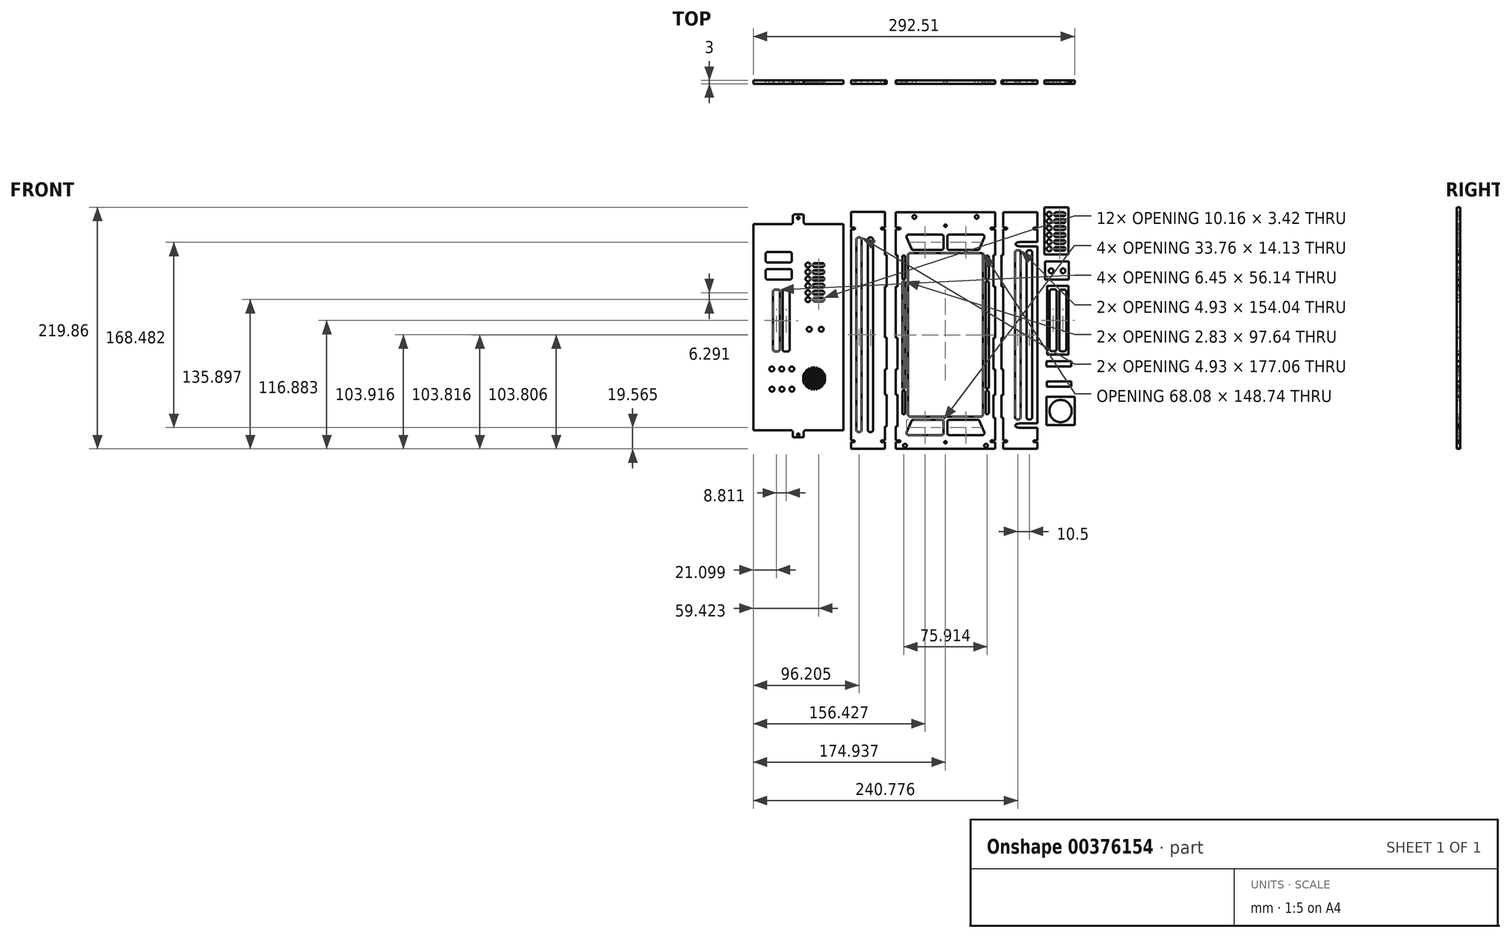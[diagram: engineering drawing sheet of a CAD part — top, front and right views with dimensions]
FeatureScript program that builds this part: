
annotation { "Feature Type Name" : "Feature", "Feature Type Description" : "" }
export const myFeature = defineFeature(function(context is Context, id is Id, definition is map)
    precondition{}
    {
        {
            var Q0;
            Q0=qCreatedBy(makeId("Front.planeOp"),FACE);
            var sketch = newSketch(context, id + "F0", { "sketchPlane" : qUnion([Q0])});
            skCircle(sketch, "E0", {"center": v(131.55, 198.45) * mm, "radius": 2.2 * mm});
            skCircle(sketch, "E1", {"center": v(131.55, 204.74) * mm, "radius": 2.2 * mm});
            skCircle(sketch, "E2", {"center": v(131.55, 211.03) * mm, "radius": 2.2 * mm});
            skCircle(sketch, "E3", {"center": v(131.55, 217.32) * mm, "radius": 2.2 * mm});
            skCircle(sketch, "E4", {"center": v(131.55, 223.61) * mm, "radius": 2.2 * mm});
            skCircle(sketch, "E5", {"center": v(131.55, 229.9) * mm, "radius": 2.2 * mm});
            skCircle(sketch, "E6", {"center": v(133.32, 178.42) * mm, "radius": 2.2 * mm});
            skCircle(sketch, "E7", {"center": v(144.17, 178.42) * mm, "radius": 2.2 * mm});
            skCircle(sketch, "E8", {"center": v(141.9, 50.82) * mm, "radius": 10.16 * mm});
            skCircle(sketch, "E9", {"center": v(37.16, 219.53) * mm, "radius": 1.07 * mm});
            skCircle(sketch, "E10", {"center": v(37.13, 22.37) * mm, "radius": 1.07 * mm});
            skCircle(sketch, "E11", {"center": v(-86.74, 125.22) * mm, "radius": 2.2 * mm});
            skCircle(sketch, "E12", {"center": v(-75.89, 125.22) * mm, "radius": 2.2 * mm});
            skCircle(sketch, "E13", {"center": v(-87.97, 152.24) * mm, "radius": 2.2 * mm});
            skCircle(sketch, "E14", {"center": v(-87.97, 158.53) * mm, "radius": 2.2 * mm});
            skCircle(sketch, "E15", {"center": v(-87.97, 164.82) * mm, "radius": 2.2 * mm});
            skCircle(sketch, "E16", {"center": v(-87.97, 171.1) * mm, "radius": 2.2 * mm});
            skCircle(sketch, "E17", {"center": v(-87.97, 177.4) * mm, "radius": 2.2 * mm});
            skCircle(sketch, "E18", {"center": v(-87.97, 183.7) * mm, "radius": 2.2 * mm});
            skCircle(sketch, "E19", {"center": v(-96.77, 226.54) * mm, "radius": 1.07 * mm});
            skCircle(sketch, "E20", {"center": v(-96.8, 29.38) * mm, "radius": 1.07 * mm});
            skCircle(sketch, "E21", {"center": v(-102.71, 89.08) * mm, "radius": 2.2 * mm});
            skCircle(sketch, "E22", {"center": v(-111.79, 89.08) * mm, "radius": 2.2 * mm});
            skCircle(sketch, "E23", {"center": v(-120.86, 89.08) * mm, "radius": 2.2 * mm});
            skCircle(sketch, "E24", {"center": v(-120.72, 70.7) * mm, "radius": 2.2 * mm});
            skCircle(sketch, "E25", {"center": v(-111.65, 70.7) * mm, "radius": 2.2 * mm});
            skCircle(sketch, "E26", {"center": v(-102.57, 70.7) * mm, "radius": 2.2 * mm});
            skLineSegment(sketch, "E27", {"start": v(73.7, 191.17) * mm, "end": v(73.7, 171.98) * mm});
            skArc(sketch, "E28", {"start": v(73.7, 171.98) * mm, "mid": v(74.01, 171.22) * mm, "end": v(74.77, 170.91) * mm});
            skLineSegment(sketch, "E29", {"start": v(74.77, 170.91) * mm, "end": v(75.46, 170.91) * mm});
            skArc(sketch, "E30", {"start": v(75.46, 170.91) * mm, "mid": v(76.21, 171.22) * mm, "end": v(76.53, 171.98) * mm});
            skLineSegment(sketch, "E31", {"start": v(76.53, 171.98) * mm, "end": v(76.53, 191.17) * mm});
            skArc(sketch, "E32", {"start": v(76.53, 191.17) * mm, "mid": v(76.21, 191.93) * mm, "end": v(75.46, 192.24) * mm});
            skLineSegment(sketch, "E33", {"start": v(75.46, 192.24) * mm, "end": v(74.77, 192.24) * mm});
            skArc(sketch, "E34", {"start": v(74.77, 192.24) * mm, "mid": v(74.01, 191.93) * mm, "end": v(73.7, 191.17) * mm});
            skLineSegment(sketch, "E35", {"start": v(73.7, 167.9) * mm, "end": v(73.7, 72.4) * mm});
            skArc(sketch, "E36", {"start": v(73.7, 72.4) * mm, "mid": v(74.01, 71.64) * mm, "end": v(74.77, 71.32) * mm});
            skLineSegment(sketch, "E37", {"start": v(74.77, 71.32) * mm, "end": v(75.46, 71.32) * mm});
            skArc(sketch, "E38", {"start": v(75.46, 71.32) * mm, "mid": v(76.21, 71.64) * mm, "end": v(76.53, 72.4) * mm});
            skLineSegment(sketch, "E39", {"start": v(76.53, 72.4) * mm, "end": v(76.53, 167.9) * mm});
            skArc(sketch, "E40", {"start": v(76.53, 167.9) * mm, "mid": v(76.21, 168.65) * mm, "end": v(75.46, 168.97) * mm});
            skLineSegment(sketch, "E41", {"start": v(75.46, 168.97) * mm, "end": v(74.77, 168.97) * mm});
            skArc(sketch, "E42", {"start": v(74.77, 168.97) * mm, "mid": v(74.01, 168.65) * mm, "end": v(73.7, 167.9) * mm});
            skLineSegment(sketch, "E43", {"start": v(73.7, 68.3) * mm, "end": v(73.7, 49.12) * mm});
            skArc(sketch, "E44", {"start": v(73.7, 49.12) * mm, "mid": v(74.01, 48.36) * mm, "end": v(74.77, 48.05) * mm});
            skLineSegment(sketch, "E45", {"start": v(74.77, 48.05) * mm, "end": v(75.46, 48.05) * mm});
            skArc(sketch, "E46", {"start": v(75.46, 48.05) * mm, "mid": v(76.21, 48.36) * mm, "end": v(76.53, 49.12) * mm});
            skLineSegment(sketch, "E47", {"start": v(76.53, 49.12) * mm, "end": v(76.53, 68.3) * mm});
            skArc(sketch, "E48", {"start": v(76.53, 68.3) * mm, "mid": v(76.21, 69.07) * mm, "end": v(75.46, 69.38) * mm});
            skLineSegment(sketch, "E49", {"start": v(75.46, 69.38) * mm, "end": v(74.77, 69.38) * mm});
            skArc(sketch, "E50", {"start": v(74.77, 69.38) * mm, "mid": v(74.01, 69.07) * mm, "end": v(73.7, 68.3) * mm});
            skArc(sketch, "E51", {"start": v(0.61, 68.3) * mm, "mid": v(0.3, 69.07) * mm, "end": v(-0.46, 69.38) * mm});
            skLineSegment(sketch, "E52", {"start": v(-0.46, 69.38) * mm, "end": v(-1.14, 69.38) * mm});
            skArc(sketch, "E53", {"start": v(-1.14, 69.38) * mm, "mid": v(-1.9, 69.07) * mm, "end": v(-2.21, 68.3) * mm});
            skLineSegment(sketch, "E54", {"start": v(-2.21, 68.3) * mm, "end": v(-2.21, 49.12) * mm});
            skArc(sketch, "E55", {"start": v(-2.21, 49.12) * mm, "mid": v(-1.9, 48.36) * mm, "end": v(-1.14, 48.05) * mm});
            skLineSegment(sketch, "E56", {"start": v(-1.14, 48.05) * mm, "end": v(-0.46, 48.05) * mm});
            skArc(sketch, "E57", {"start": v(-0.46, 48.05) * mm, "mid": v(0.3, 48.36) * mm, "end": v(0.61, 49.12) * mm});
            skLineSegment(sketch, "E58", {"start": v(0.61, 49.12) * mm, "end": v(0.61, 68.3) * mm});
            skArc(sketch, "E59", {"start": v(0.61, 167.9) * mm, "mid": v(0.3, 168.65) * mm, "end": v(-0.46, 168.97) * mm});
            skLineSegment(sketch, "E60", {"start": v(-0.46, 168.97) * mm, "end": v(-1.14, 168.97) * mm});
            skArc(sketch, "E61", {"start": v(-1.14, 168.97) * mm, "mid": v(-1.9, 168.65) * mm, "end": v(-2.21, 167.9) * mm});
            skLineSegment(sketch, "E62", {"start": v(-2.21, 167.9) * mm, "end": v(-2.21, 72.4) * mm});
            skArc(sketch, "E63", {"start": v(-2.21, 72.4) * mm, "mid": v(-1.9, 71.64) * mm, "end": v(-1.14, 71.32) * mm});
            skLineSegment(sketch, "E64", {"start": v(-1.14, 71.32) * mm, "end": v(-0.46, 71.32) * mm});
            skArc(sketch, "E65", {"start": v(-0.46, 71.32) * mm, "mid": v(0.3, 71.64) * mm, "end": v(0.61, 72.4) * mm});
            skLineSegment(sketch, "E66", {"start": v(0.61, 72.4) * mm, "end": v(0.61, 167.9) * mm});
            skArc(sketch, "E67", {"start": v(0.61, 191.17) * mm, "mid": v(0.3, 191.93) * mm, "end": v(-0.46, 192.24) * mm});
            skLineSegment(sketch, "E68", {"start": v(-0.46, 192.24) * mm, "end": v(-1.14, 192.24) * mm});
            skArc(sketch, "E69", {"start": v(-1.14, 192.24) * mm, "mid": v(-1.9, 191.93) * mm, "end": v(-2.21, 191.17) * mm});
            skLineSegment(sketch, "E70", {"start": v(-2.21, 191.17) * mm, "end": v(-2.21, 171.98) * mm});
            skArc(sketch, "E71", {"start": v(-2.21, 171.98) * mm, "mid": v(-1.9, 171.22) * mm, "end": v(-1.14, 170.91) * mm});
            skLineSegment(sketch, "E72", {"start": v(-1.14, 170.91) * mm, "end": v(-0.46, 170.91) * mm});
            skArc(sketch, "E73", {"start": v(-0.46, 170.91) * mm, "mid": v(0.3, 171.22) * mm, "end": v(0.61, 171.98) * mm});
            skLineSegment(sketch, "E74", {"start": v(0.61, 171.98) * mm, "end": v(0.61, 191.17) * mm});
            skLineSegment(sketch, "E75", {"start": v(8.26, 197.32) * mm, "end": v(33.27, 197.32) * mm});
            skArc(sketch, "E76", {"start": v(33.27, 197.32) * mm, "mid": v(33.63, 197.35) * mm, "end": v(33.98, 197.42) * mm});
            skArc(sketch, "E77", {"start": v(33.98, 197.42) * mm, "mid": v(34.3, 197.53) * mm, "end": v(34.6, 197.69) * mm});
            skArc(sketch, "E78", {"start": v(34.6, 197.69) * mm, "mid": v(34.85, 197.86) * mm, "end": v(35.06, 198.06) * mm});
            skArc(sketch, "E79", {"start": v(35.06, 198.06) * mm, "mid": v(35.22, 198.26) * mm, "end": v(35.35, 198.48) * mm});
            skArc(sketch, "E80", {"start": v(35.35, 198.48) * mm, "mid": v(35.44, 198.7) * mm, "end": v(35.5, 198.92) * mm});
            skArc(sketch, "E81", {"start": v(35.5, 198.92) * mm, "mid": v(35.52, 199.07) * mm, "end": v(35.53, 199.21) * mm});
            skLineSegment(sketch, "E82", {"start": v(35.53, 199.21) * mm, "end": v(35.53, 209.56) * mm});
            skArc(sketch, "E83", {"start": v(35.53, 209.56) * mm, "mid": v(35.51, 209.79) * mm, "end": v(35.46, 210) * mm});
            skArc(sketch, "E84", {"start": v(35.46, 210) * mm, "mid": v(35.38, 210.22) * mm, "end": v(35.28, 210.43) * mm});
            skArc(sketch, "E85", {"start": v(35.28, 210.43) * mm, "mid": v(35.12, 210.65) * mm, "end": v(34.93, 210.84) * mm});
            skArc(sketch, "E86", {"start": v(34.93, 210.84) * mm, "mid": v(34.7, 211.03) * mm, "end": v(34.43, 211.18) * mm});
            skArc(sketch, "E87", {"start": v(34.43, 211.18) * mm, "mid": v(34.11, 211.32) * mm, "end": v(33.78, 211.4) * mm});
            skArc(sketch, "E88", {"start": v(33.78, 211.4) * mm, "mid": v(33.52, 211.44) * mm, "end": v(33.27, 211.45) * mm});
            skLineSegment(sketch, "E89", {"start": v(33.27, 211.45) * mm, "end": v(4.02, 211.45) * mm});
            skArc(sketch, "E90", {"start": v(4.02, 211.45) * mm, "mid": v(3.66, 211.43) * mm, "end": v(3.31, 211.35) * mm});
            skArc(sketch, "E91", {"start": v(3.31, 211.35) * mm, "mid": v(3, 211.24) * mm, "end": v(2.7, 211.09) * mm});
            skArc(sketch, "E92", {"start": v(2.7, 211.09) * mm, "mid": v(2.45, 210.91) * mm, "end": v(2.23, 210.7) * mm});
            skArc(sketch, "E93", {"start": v(2.23, 210.7) * mm, "mid": v(2.07, 210.5) * mm, "end": v(1.94, 210.29) * mm});
            skArc(sketch, "E94", {"start": v(1.94, 210.29) * mm, "mid": v(1.85, 210.07) * mm, "end": v(1.8, 209.85) * mm});
            skArc(sketch, "E95", {"start": v(1.8, 209.85) * mm, "mid": v(1.77, 209.7) * mm, "end": v(1.77, 209.56) * mm});
            skLineSegment(sketch, "E96", {"start": v(1.77, 209.56) * mm, "end": v(1.77, 209.55) * mm});
            skArc(sketch, "E97", {"start": v(1.77, 209.55) * mm, "mid": v(1.78, 209.34) * mm, "end": v(1.82, 209.14) * mm});
            skArc(sketch, "E98", {"start": v(1.82, 209.14) * mm, "mid": v(1.85, 209.04) * mm, "end": v(1.89, 208.95) * mm});
            skLineSegment(sketch, "E99", {"start": v(1.89, 208.95) * mm, "end": v(6.13, 198.6) * mm});
            skArc(sketch, "E100", {"start": v(6.13, 198.6) * mm, "mid": v(6.23, 198.38) * mm, "end": v(6.37, 198.18) * mm});
            skArc(sketch, "E101", {"start": v(6.37, 198.18) * mm, "mid": v(6.56, 197.97) * mm, "end": v(6.77, 197.8) * mm});
            skArc(sketch, "E102", {"start": v(6.77, 197.8) * mm, "mid": v(7.05, 197.62) * mm, "end": v(7.34, 197.49) * mm});
            skArc(sketch, "E103", {"start": v(7.34, 197.49) * mm, "mid": v(7.68, 197.39) * mm, "end": v(8.04, 197.33) * mm});
            skArc(sketch, "E104", {"start": v(8.04, 197.33) * mm, "mid": v(8.15, 197.33) * mm, "end": v(8.26, 197.32) * mm});
            skLineSegment(sketch, "E105", {"start": v(70.3, 211.45) * mm, "end": v(41.04, 211.45) * mm});
            skArc(sketch, "E106", {"start": v(41.04, 211.45) * mm, "mid": v(40.68, 211.43) * mm, "end": v(40.33, 211.35) * mm});
            skArc(sketch, "E107", {"start": v(40.33, 211.35) * mm, "mid": v(40.01, 211.24) * mm, "end": v(39.71, 211.09) * mm});
            skArc(sketch, "E108", {"start": v(39.71, 211.09) * mm, "mid": v(39.47, 210.91) * mm, "end": v(39.25, 210.7) * mm});
            skArc(sketch, "E109", {"start": v(39.25, 210.7) * mm, "mid": v(39.1, 210.5) * mm, "end": v(38.96, 210.29) * mm});
            skArc(sketch, "E110", {"start": v(38.96, 210.29) * mm, "mid": v(38.87, 210.07) * mm, "end": v(38.81, 209.85) * mm});
            skArc(sketch, "E111", {"start": v(38.81, 209.85) * mm, "mid": v(38.8, 209.7) * mm, "end": v(38.79, 209.56) * mm});
            skLineSegment(sketch, "E112", {"start": v(38.79, 209.56) * mm, "end": v(38.79, 199.21) * mm});
            skArc(sketch, "E113", {"start": v(38.79, 199.21) * mm, "mid": v(38.8, 198.99) * mm, "end": v(38.85, 198.77) * mm});
            skArc(sketch, "E114", {"start": v(38.85, 198.77) * mm, "mid": v(38.93, 198.55) * mm, "end": v(39.04, 198.34) * mm});
            skArc(sketch, "E115", {"start": v(39.04, 198.34) * mm, "mid": v(39.2, 198.13) * mm, "end": v(39.38, 197.93) * mm});
            skArc(sketch, "E116", {"start": v(39.38, 197.93) * mm, "mid": v(39.62, 197.74) * mm, "end": v(39.89, 197.59) * mm});
            skArc(sketch, "E117", {"start": v(39.89, 197.59) * mm, "mid": v(40.2, 197.46) * mm, "end": v(40.54, 197.37) * mm});
            skArc(sketch, "E118", {"start": v(40.54, 197.37) * mm, "mid": v(40.79, 197.33) * mm, "end": v(41.04, 197.32) * mm});
            skLineSegment(sketch, "E119", {"start": v(41.04, 197.32) * mm, "end": v(66.05, 197.32) * mm});
            skArc(sketch, "E120", {"start": v(66.05, 197.32) * mm, "mid": v(66.41, 197.35) * mm, "end": v(66.76, 197.42) * mm});
            skArc(sketch, "E121", {"start": v(66.76, 197.42) * mm, "mid": v(67.08, 197.53) * mm, "end": v(67.37, 197.68) * mm});
            skArc(sketch, "E122", {"start": v(67.37, 197.68) * mm, "mid": v(67.61, 197.85) * mm, "end": v(67.83, 198.05) * mm});
            skArc(sketch, "E123", {"start": v(67.83, 198.05) * mm, "mid": v(68, 198.26) * mm, "end": v(68.13, 198.48) * mm});
            skArc(sketch, "E124", {"start": v(68.13, 198.48) * mm, "mid": v(68.16, 198.54) * mm, "end": v(68.19, 198.6) * mm});
            skLineSegment(sketch, "E125", {"start": v(68.19, 198.6) * mm, "end": v(72.43, 208.95) * mm});
            skArc(sketch, "E126", {"start": v(72.43, 208.95) * mm, "mid": v(72.5, 209.16) * mm, "end": v(72.54, 209.39) * mm});
            skArc(sketch, "E127", {"start": v(72.54, 209.39) * mm, "mid": v(72.55, 209.6) * mm, "end": v(72.53, 209.82) * mm});
            skArc(sketch, "E128", {"start": v(72.53, 209.82) * mm, "mid": v(72.47, 210.04) * mm, "end": v(72.4, 210.25) * mm});
            skArc(sketch, "E129", {"start": v(72.4, 210.25) * mm, "mid": v(72.27, 210.47) * mm, "end": v(72.11, 210.67) * mm});
            skArc(sketch, "E130", {"start": v(72.11, 210.67) * mm, "mid": v(71.9, 210.88) * mm, "end": v(71.68, 211.05) * mm});
            skArc(sketch, "E131", {"start": v(71.68, 211.05) * mm, "mid": v(71.38, 211.22) * mm, "end": v(71.07, 211.33) * mm});
            skLineSegment(sketch, "E132", {"start": v(71.07, 211.33) * mm, "end": v(71.02, 211.35) * mm});
            skArc(sketch, "E133", {"start": v(71.02, 211.35) * mm, "mid": v(70.69, 211.42) * mm, "end": v(70.35, 211.45) * mm});
            skLineSegment(sketch, "E134", {"start": v(70.35, 211.45) * mm, "end": v(70.3, 211.45) * mm});
            skArc(sketch, "E135", {"start": v(70.3, 28.84) * mm, "mid": v(70.65, 28.86) * mm, "end": v(71, 28.94) * mm});
            skArc(sketch, "E136", {"start": v(71, 28.94) * mm, "mid": v(71.32, 29.05) * mm, "end": v(71.62, 29.2) * mm});
            skArc(sketch, "E137", {"start": v(71.62, 29.2) * mm, "mid": v(71.87, 29.38) * mm, "end": v(72.08, 29.58) * mm});
            skArc(sketch, "E138", {"start": v(72.08, 29.58) * mm, "mid": v(72.24, 29.78) * mm, "end": v(72.37, 30) * mm});
            skArc(sketch, "E139", {"start": v(72.37, 30) * mm, "mid": v(72.46, 30.22) * mm, "end": v(72.52, 30.44) * mm});
            skArc(sketch, "E140", {"start": v(72.52, 30.44) * mm, "mid": v(72.54, 30.59) * mm, "end": v(72.55, 30.73) * mm});
            skArc(sketch, "E141", {"start": v(72.55, 30.73) * mm, "mid": v(72.53, 30.94) * mm, "end": v(72.5, 31.15) * mm});
            skArc(sketch, "E142", {"start": v(72.5, 31.15) * mm, "mid": v(72.46, 31.24) * mm, "end": v(72.43, 31.34) * mm});
            skLineSegment(sketch, "E143", {"start": v(72.43, 31.34) * mm, "end": v(68.19, 41.7) * mm});
            skArc(sketch, "E144", {"start": v(68.19, 41.7) * mm, "mid": v(68.08, 41.9) * mm, "end": v(67.94, 42.11) * mm});
            skArc(sketch, "E145", {"start": v(67.94, 42.11) * mm, "mid": v(67.76, 42.32) * mm, "end": v(67.54, 42.5) * mm});
            skArc(sketch, "E146", {"start": v(67.54, 42.5) * mm, "mid": v(67.27, 42.67) * mm, "end": v(66.97, 42.8) * mm});
            skArc(sketch, "E147", {"start": v(66.97, 42.8) * mm, "mid": v(66.63, 42.9) * mm, "end": v(66.28, 42.96) * mm});
            skArc(sketch, "E148", {"start": v(66.28, 42.96) * mm, "mid": v(66.16, 42.97) * mm, "end": v(66.05, 42.97) * mm});
            skLineSegment(sketch, "E149", {"start": v(66.05, 42.97) * mm, "end": v(41.04, 42.97) * mm});
            skArc(sketch, "E150", {"start": v(41.04, 42.97) * mm, "mid": v(40.68, 42.95) * mm, "end": v(40.33, 42.87) * mm});
            skArc(sketch, "E151", {"start": v(40.33, 42.87) * mm, "mid": v(40.01, 42.76) * mm, "end": v(39.71, 42.6) * mm});
            skArc(sketch, "E152", {"start": v(39.71, 42.6) * mm, "mid": v(39.47, 42.43) * mm, "end": v(39.25, 42.23) * mm});
            skArc(sketch, "E153", {"start": v(39.25, 42.23) * mm, "mid": v(39.1, 42.03) * mm, "end": v(38.96, 41.8) * mm});
            skArc(sketch, "E154", {"start": v(38.96, 41.8) * mm, "mid": v(38.87, 41.6) * mm, "end": v(38.81, 41.37) * mm});
            skArc(sketch, "E155", {"start": v(38.81, 41.37) * mm, "mid": v(38.8, 41.22) * mm, "end": v(38.79, 41.08) * mm});
            skLineSegment(sketch, "E156", {"start": v(38.79, 41.08) * mm, "end": v(38.79, 30.73) * mm});
            skArc(sketch, "E157", {"start": v(38.79, 30.73) * mm, "mid": v(38.8, 30.5) * mm, "end": v(38.85, 30.29) * mm});
            skArc(sketch, "E158", {"start": v(38.85, 30.29) * mm, "mid": v(38.93, 30.07) * mm, "end": v(39.04, 29.86) * mm});
            skArc(sketch, "E159", {"start": v(39.04, 29.86) * mm, "mid": v(39.2, 29.64) * mm, "end": v(39.38, 29.45) * mm});
            skArc(sketch, "E160", {"start": v(39.38, 29.45) * mm, "mid": v(39.62, 29.26) * mm, "end": v(39.89, 29.1) * mm});
            skArc(sketch, "E161", {"start": v(39.89, 29.1) * mm, "mid": v(40.2, 28.98) * mm, "end": v(40.54, 28.89) * mm});
            skArc(sketch, "E162", {"start": v(40.54, 28.89) * mm, "mid": v(40.79, 28.85) * mm, "end": v(41.04, 28.84) * mm});
            skLineSegment(sketch, "E163", {"start": v(41.04, 28.84) * mm, "end": v(70.3, 28.84) * mm});
            skLineSegment(sketch, "E164", {"start": v(4.02, 28.84) * mm, "end": v(33.27, 28.84) * mm});
            skArc(sketch, "E165", {"start": v(33.27, 28.84) * mm, "mid": v(33.63, 28.86) * mm, "end": v(33.98, 28.94) * mm});
            skArc(sketch, "E166", {"start": v(33.98, 28.94) * mm, "mid": v(34.3, 29.05) * mm, "end": v(34.6, 29.2) * mm});
            skArc(sketch, "E167", {"start": v(34.6, 29.2) * mm, "mid": v(34.85, 29.38) * mm, "end": v(35.06, 29.58) * mm});
            skArc(sketch, "E168", {"start": v(35.06, 29.58) * mm, "mid": v(35.22, 29.78) * mm, "end": v(35.35, 30) * mm});
            skArc(sketch, "E169", {"start": v(35.35, 30) * mm, "mid": v(35.44, 30.22) * mm, "end": v(35.5, 30.44) * mm});
            skArc(sketch, "E170", {"start": v(35.5, 30.44) * mm, "mid": v(35.52, 30.59) * mm, "end": v(35.53, 30.73) * mm});
            skLineSegment(sketch, "E171", {"start": v(35.53, 30.73) * mm, "end": v(35.53, 41.08) * mm});
            skArc(sketch, "E172", {"start": v(35.53, 41.08) * mm, "mid": v(35.51, 41.3) * mm, "end": v(35.46, 41.52) * mm});
            skArc(sketch, "E173", {"start": v(35.46, 41.52) * mm, "mid": v(35.38, 41.74) * mm, "end": v(35.28, 41.95) * mm});
            skArc(sketch, "E174", {"start": v(35.28, 41.95) * mm, "mid": v(35.12, 42.17) * mm, "end": v(34.93, 42.36) * mm});
            skArc(sketch, "E175", {"start": v(34.93, 42.36) * mm, "mid": v(34.7, 42.55) * mm, "end": v(34.43, 42.7) * mm});
            skArc(sketch, "E176", {"start": v(34.43, 42.7) * mm, "mid": v(34.11, 42.83) * mm, "end": v(33.78, 42.92) * mm});
            skArc(sketch, "E177", {"start": v(33.78, 42.92) * mm, "mid": v(33.52, 42.96) * mm, "end": v(33.27, 42.97) * mm});
            skLineSegment(sketch, "E178", {"start": v(33.27, 42.97) * mm, "end": v(8.26, 42.97) * mm});
            skArc(sketch, "E179", {"start": v(8.26, 42.97) * mm, "mid": v(7.9, 42.94) * mm, "end": v(7.53, 42.86) * mm});
            skArc(sketch, "E180", {"start": v(7.53, 42.86) * mm, "mid": v(7.21, 42.75) * mm, "end": v(6.91, 42.6) * mm});
            skArc(sketch, "E181", {"start": v(6.91, 42.6) * mm, "mid": v(6.68, 42.43) * mm, "end": v(6.47, 42.23) * mm});
            skArc(sketch, "E182", {"start": v(6.47, 42.23) * mm, "mid": v(6.31, 42.03) * mm, "end": v(6.18, 41.81) * mm});
            skArc(sketch, "E183", {"start": v(6.18, 41.81) * mm, "mid": v(6.15, 41.75) * mm, "end": v(6.13, 41.7) * mm});
            skLineSegment(sketch, "E184", {"start": v(6.13, 41.7) * mm, "end": v(1.89, 31.34) * mm});
            skArc(sketch, "E185", {"start": v(1.89, 31.34) * mm, "mid": v(1.82, 31.15) * mm, "end": v(1.78, 30.95) * mm});
            skArc(sketch, "E186", {"start": v(1.78, 30.95) * mm, "mid": v(1.77, 30.84) * mm, "end": v(1.77, 30.73) * mm});
            skArc(sketch, "E187", {"start": v(1.77, 30.73) * mm, "mid": v(1.78, 30.5) * mm, "end": v(1.83, 30.29) * mm});
            skArc(sketch, "E188", {"start": v(1.83, 30.29) * mm, "mid": v(1.9, 30.07) * mm, "end": v(2.02, 29.86) * mm});
            skArc(sketch, "E189", {"start": v(2.02, 29.86) * mm, "mid": v(2.18, 29.64) * mm, "end": v(2.36, 29.45) * mm});
            skArc(sketch, "E190", {"start": v(2.36, 29.45) * mm, "mid": v(2.6, 29.26) * mm, "end": v(2.86, 29.1) * mm});
            skArc(sketch, "E191", {"start": v(2.86, 29.1) * mm, "mid": v(3.18, 28.98) * mm, "end": v(3.52, 28.89) * mm});
            skArc(sketch, "E192", {"start": v(3.52, 28.89) * mm, "mid": v(3.77, 28.85) * mm, "end": v(4.02, 28.84) * mm});
            skLineSegment(sketch, "E193", {"start": v(127.14, 236.2) * mm, "end": v(127.14, 193.3) * mm});
            skLineSegment(sketch, "E194", {"start": v(127.14, 193.3) * mm, "end": v(149.08, 193.3) * mm});
            skLineSegment(sketch, "E195", {"start": v(149.08, 193.3) * mm, "end": v(149.08, 236.2) * mm});
            skLineSegment(sketch, "E196", {"start": v(149.08, 236.2) * mm, "end": v(127.14, 236.2) * mm});
            skLineSegment(sketch, "E197", {"start": v(136.09, 230.39) * mm, "end": v(136.09, 229.41) * mm});
            skArc(sketch, "E198", {"start": v(136.09, 229.41) * mm, "mid": v(136.1, 229.28) * mm, "end": v(136.12, 229.15) * mm});
            skArc(sketch, "E199", {"start": v(136.12, 229.15) * mm, "mid": v(136.17, 229.01) * mm, "end": v(136.24, 228.89) * mm});
            skArc(sketch, "E200", {"start": v(136.24, 228.89) * mm, "mid": v(136.34, 228.75) * mm, "end": v(136.46, 228.62) * mm});
            skArc(sketch, "E201", {"start": v(136.46, 228.62) * mm, "mid": v(136.63, 228.5) * mm, "end": v(136.8, 228.38) * mm});
            skArc(sketch, "E202", {"start": v(136.8, 228.38) * mm, "mid": v(137.04, 228.29) * mm, "end": v(137.29, 228.23) * mm});
            skArc(sketch, "E203", {"start": v(137.29, 228.23) * mm, "mid": v(137.47, 228.2) * mm, "end": v(137.66, 228.2) * mm});
            skLineSegment(sketch, "E204", {"start": v(137.66, 228.2) * mm, "end": v(144.67, 228.2) * mm});
            skArc(sketch, "E205", {"start": v(144.67, 228.2) * mm, "mid": v(144.94, 228.2) * mm, "end": v(145.2, 228.26) * mm});
            skArc(sketch, "E206", {"start": v(145.2, 228.26) * mm, "mid": v(145.43, 228.34) * mm, "end": v(145.64, 228.45) * mm});
            skArc(sketch, "E207", {"start": v(145.64, 228.45) * mm, "mid": v(145.8, 228.56) * mm, "end": v(145.95, 228.7) * mm});
            skArc(sketch, "E208", {"start": v(145.95, 228.7) * mm, "mid": v(146.05, 228.83) * mm, "end": v(146.14, 228.97) * mm});
            skArc(sketch, "E209", {"start": v(146.14, 228.97) * mm, "mid": v(146.2, 229.1) * mm, "end": v(146.23, 229.23) * mm});
            skArc(sketch, "E210", {"start": v(146.23, 229.23) * mm, "mid": v(146.24, 229.32) * mm, "end": v(146.24, 229.41) * mm});
            skLineSegment(sketch, "E211", {"start": v(146.24, 229.41) * mm, "end": v(146.24, 230.39) * mm});
            skArc(sketch, "E212", {"start": v(146.24, 230.39) * mm, "mid": v(146.24, 230.52) * mm, "end": v(146.2, 230.65) * mm});
            skArc(sketch, "E213", {"start": v(146.2, 230.65) * mm, "mid": v(146.16, 230.79) * mm, "end": v(146.1, 230.92) * mm});
            skArc(sketch, "E214", {"start": v(146.1, 230.92) * mm, "mid": v(146, 231.06) * mm, "end": v(145.87, 231.18) * mm});
            skArc(sketch, "E215", {"start": v(145.87, 231.18) * mm, "mid": v(145.7, 231.31) * mm, "end": v(145.52, 231.42) * mm});
            skArc(sketch, "E216", {"start": v(145.52, 231.42) * mm, "mid": v(145.29, 231.51) * mm, "end": v(145.04, 231.58) * mm});
            skArc(sketch, "E217", {"start": v(145.04, 231.58) * mm, "mid": v(144.86, 231.6) * mm, "end": v(144.67, 231.61) * mm});
            skLineSegment(sketch, "E218", {"start": v(144.67, 231.61) * mm, "end": v(137.66, 231.61) * mm});
            skArc(sketch, "E219", {"start": v(137.66, 231.61) * mm, "mid": v(137.4, 231.6) * mm, "end": v(137.13, 231.54) * mm});
            skArc(sketch, "E220", {"start": v(137.13, 231.54) * mm, "mid": v(136.9, 231.46) * mm, "end": v(136.7, 231.35) * mm});
            skArc(sketch, "E221", {"start": v(136.7, 231.35) * mm, "mid": v(136.53, 231.24) * mm, "end": v(136.38, 231.1) * mm});
            skArc(sketch, "E222", {"start": v(136.38, 231.1) * mm, "mid": v(136.28, 230.97) * mm, "end": v(136.2, 230.83) * mm});
            skArc(sketch, "E223", {"start": v(136.2, 230.83) * mm, "mid": v(136.14, 230.7) * mm, "end": v(136.1, 230.57) * mm});
            skArc(sketch, "E224", {"start": v(136.1, 230.57) * mm, "mid": v(136.09, 230.48) * mm, "end": v(136.09, 230.39) * mm});
            skLineSegment(sketch, "E225", {"start": v(136.09, 224.1) * mm, "end": v(136.09, 223.12) * mm});
            skArc(sketch, "E226", {"start": v(136.09, 223.12) * mm, "mid": v(136.1, 222.99) * mm, "end": v(136.12, 222.86) * mm});
            skArc(sketch, "E227", {"start": v(136.12, 222.86) * mm, "mid": v(136.17, 222.72) * mm, "end": v(136.24, 222.6) * mm});
            skArc(sketch, "E228", {"start": v(136.24, 222.6) * mm, "mid": v(136.34, 222.46) * mm, "end": v(136.46, 222.33) * mm});
            skArc(sketch, "E229", {"start": v(136.46, 222.33) * mm, "mid": v(136.63, 222.2) * mm, "end": v(136.8, 222.1) * mm});
            skArc(sketch, "E230", {"start": v(136.8, 222.1) * mm, "mid": v(137.04, 222) * mm, "end": v(137.29, 221.93) * mm});
            skArc(sketch, "E231", {"start": v(137.29, 221.93) * mm, "mid": v(137.47, 221.9) * mm, "end": v(137.66, 221.9) * mm});
            skLineSegment(sketch, "E232", {"start": v(137.66, 221.9) * mm, "end": v(144.67, 221.9) * mm});
            skArc(sketch, "E233", {"start": v(144.67, 221.9) * mm, "mid": v(144.94, 221.92) * mm, "end": v(145.2, 221.97) * mm});
            skArc(sketch, "E234", {"start": v(145.2, 221.97) * mm, "mid": v(145.43, 222.05) * mm, "end": v(145.64, 222.16) * mm});
            skArc(sketch, "E235", {"start": v(145.64, 222.16) * mm, "mid": v(145.8, 222.27) * mm, "end": v(145.95, 222.41) * mm});
            skArc(sketch, "E236", {"start": v(145.95, 222.41) * mm, "mid": v(146.05, 222.54) * mm, "end": v(146.14, 222.68) * mm});
            skArc(sketch, "E237", {"start": v(146.14, 222.68) * mm, "mid": v(146.2, 222.8) * mm, "end": v(146.23, 222.94) * mm});
            skArc(sketch, "E238", {"start": v(146.23, 222.94) * mm, "mid": v(146.24, 223.03) * mm, "end": v(146.24, 223.12) * mm});
            skLineSegment(sketch, "E239", {"start": v(146.24, 223.12) * mm, "end": v(146.24, 224.1) * mm});
            skArc(sketch, "E240", {"start": v(146.24, 224.1) * mm, "mid": v(146.24, 224.23) * mm, "end": v(146.2, 224.36) * mm});
            skArc(sketch, "E241", {"start": v(146.2, 224.36) * mm, "mid": v(146.16, 224.5) * mm, "end": v(146.1, 224.63) * mm});
            skArc(sketch, "E242", {"start": v(146.1, 224.63) * mm, "mid": v(146, 224.76) * mm, "end": v(145.87, 224.89) * mm});
            skArc(sketch, "E243", {"start": v(145.87, 224.89) * mm, "mid": v(145.7, 225.02) * mm, "end": v(145.52, 225.13) * mm});
            skArc(sketch, "E244", {"start": v(145.52, 225.13) * mm, "mid": v(145.29, 225.22) * mm, "end": v(145.04, 225.29) * mm});
            skArc(sketch, "E245", {"start": v(145.04, 225.29) * mm, "mid": v(144.86, 225.31) * mm, "end": v(144.67, 225.32) * mm});
            skLineSegment(sketch, "E246", {"start": v(144.67, 225.32) * mm, "end": v(137.66, 225.32) * mm});
            skArc(sketch, "E247", {"start": v(137.66, 225.32) * mm, "mid": v(137.4, 225.3) * mm, "end": v(137.13, 225.25) * mm});
            skArc(sketch, "E248", {"start": v(137.13, 225.25) * mm, "mid": v(136.9, 225.17) * mm, "end": v(136.7, 225.06) * mm});
            skArc(sketch, "E249", {"start": v(136.7, 225.06) * mm, "mid": v(136.53, 224.95) * mm, "end": v(136.38, 224.8) * mm});
            skArc(sketch, "E250", {"start": v(136.38, 224.8) * mm, "mid": v(136.28, 224.68) * mm, "end": v(136.2, 224.54) * mm});
            skArc(sketch, "E251", {"start": v(136.2, 224.54) * mm, "mid": v(136.14, 224.42) * mm, "end": v(136.1, 224.28) * mm});
            skArc(sketch, "E252", {"start": v(136.1, 224.28) * mm, "mid": v(136.09, 224.2) * mm, "end": v(136.09, 224.1) * mm});
            skLineSegment(sketch, "E253", {"start": v(136.09, 211.52) * mm, "end": v(136.09, 210.54) * mm});
            skArc(sketch, "E254", {"start": v(136.09, 210.54) * mm, "mid": v(136.1, 210.4) * mm, "end": v(136.12, 210.28) * mm});
            skArc(sketch, "E255", {"start": v(136.12, 210.28) * mm, "mid": v(136.17, 210.14) * mm, "end": v(136.24, 210.01) * mm});
            skArc(sketch, "E256", {"start": v(136.24, 210.01) * mm, "mid": v(136.34, 209.87) * mm, "end": v(136.46, 209.75) * mm});
            skArc(sketch, "E257", {"start": v(136.46, 209.75) * mm, "mid": v(136.63, 209.62) * mm, "end": v(136.8, 209.51) * mm});
            skArc(sketch, "E258", {"start": v(136.8, 209.51) * mm, "mid": v(137.04, 209.42) * mm, "end": v(137.29, 209.35) * mm});
            skArc(sketch, "E259", {"start": v(137.29, 209.35) * mm, "mid": v(137.47, 209.33) * mm, "end": v(137.66, 209.32) * mm});
            skLineSegment(sketch, "E260", {"start": v(137.66, 209.32) * mm, "end": v(144.67, 209.32) * mm});
            skArc(sketch, "E261", {"start": v(144.67, 209.32) * mm, "mid": v(144.94, 209.34) * mm, "end": v(145.2, 209.39) * mm});
            skArc(sketch, "E262", {"start": v(145.2, 209.39) * mm, "mid": v(145.43, 209.47) * mm, "end": v(145.64, 209.58) * mm});
            skArc(sketch, "E263", {"start": v(145.64, 209.58) * mm, "mid": v(145.8, 209.7) * mm, "end": v(145.95, 209.83) * mm});
            skArc(sketch, "E264", {"start": v(145.95, 209.83) * mm, "mid": v(146.05, 209.96) * mm, "end": v(146.14, 210.1) * mm});
            skArc(sketch, "E265", {"start": v(146.14, 210.1) * mm, "mid": v(146.2, 210.22) * mm, "end": v(146.23, 210.35) * mm});
            skArc(sketch, "E266", {"start": v(146.23, 210.35) * mm, "mid": v(146.24, 210.45) * mm, "end": v(146.24, 210.54) * mm});
            skLineSegment(sketch, "E267", {"start": v(146.24, 210.54) * mm, "end": v(146.24, 211.52) * mm});
            skArc(sketch, "E268", {"start": v(146.24, 211.52) * mm, "mid": v(146.24, 211.65) * mm, "end": v(146.2, 211.78) * mm});
            skArc(sketch, "E269", {"start": v(146.2, 211.78) * mm, "mid": v(146.16, 211.92) * mm, "end": v(146.1, 212.04) * mm});
            skArc(sketch, "E270", {"start": v(146.1, 212.04) * mm, "mid": v(146, 212.18) * mm, "end": v(145.87, 212.3) * mm});
            skArc(sketch, "E271", {"start": v(145.87, 212.3) * mm, "mid": v(145.7, 212.44) * mm, "end": v(145.52, 212.54) * mm});
            skArc(sketch, "E272", {"start": v(145.52, 212.54) * mm, "mid": v(145.29, 212.64) * mm, "end": v(145.04, 212.7) * mm});
            skArc(sketch, "E273", {"start": v(145.04, 212.7) * mm, "mid": v(144.86, 212.73) * mm, "end": v(144.67, 212.74) * mm});
            skLineSegment(sketch, "E274", {"start": v(144.67, 212.74) * mm, "end": v(137.66, 212.74) * mm});
            skArc(sketch, "E275", {"start": v(137.66, 212.74) * mm, "mid": v(137.4, 212.72) * mm, "end": v(137.13, 212.67) * mm});
            skArc(sketch, "E276", {"start": v(137.13, 212.67) * mm, "mid": v(136.9, 212.59) * mm, "end": v(136.7, 212.48) * mm});
            skArc(sketch, "E277", {"start": v(136.7, 212.48) * mm, "mid": v(136.53, 212.36) * mm, "end": v(136.38, 212.23) * mm});
            skArc(sketch, "E278", {"start": v(136.38, 212.23) * mm, "mid": v(136.28, 212.1) * mm, "end": v(136.2, 211.96) * mm});
            skArc(sketch, "E279", {"start": v(136.2, 211.96) * mm, "mid": v(136.14, 211.84) * mm, "end": v(136.1, 211.7) * mm});
            skArc(sketch, "E280", {"start": v(136.1, 211.7) * mm, "mid": v(136.09, 211.6) * mm, "end": v(136.09, 211.52) * mm});
            skLineSegment(sketch, "E281", {"start": v(136.09, 217.8) * mm, "end": v(136.09, 216.83) * mm});
            skArc(sketch, "E282", {"start": v(136.09, 216.83) * mm, "mid": v(136.1, 216.7) * mm, "end": v(136.12, 216.57) * mm});
            skArc(sketch, "E283", {"start": v(136.12, 216.57) * mm, "mid": v(136.17, 216.43) * mm, "end": v(136.24, 216.3) * mm});
            skArc(sketch, "E284", {"start": v(136.24, 216.3) * mm, "mid": v(136.34, 216.16) * mm, "end": v(136.46, 216.04) * mm});
            skArc(sketch, "E285", {"start": v(136.46, 216.04) * mm, "mid": v(136.63, 215.9) * mm, "end": v(136.8, 215.8) * mm});
            skArc(sketch, "E286", {"start": v(136.8, 215.8) * mm, "mid": v(137.04, 215.7) * mm, "end": v(137.29, 215.64) * mm});
            skArc(sketch, "E287", {"start": v(137.29, 215.64) * mm, "mid": v(137.47, 215.62) * mm, "end": v(137.66, 215.6) * mm});
            skLineSegment(sketch, "E288", {"start": v(137.66, 215.6) * mm, "end": v(144.67, 215.6) * mm});
            skArc(sketch, "E289", {"start": v(144.67, 215.6) * mm, "mid": v(144.94, 215.63) * mm, "end": v(145.2, 215.68) * mm});
            skArc(sketch, "E290", {"start": v(145.2, 215.68) * mm, "mid": v(145.43, 215.76) * mm, "end": v(145.64, 215.87) * mm});
            skArc(sketch, "E291", {"start": v(145.64, 215.87) * mm, "mid": v(145.8, 215.98) * mm, "end": v(145.95, 216.12) * mm});
            skArc(sketch, "E292", {"start": v(145.95, 216.12) * mm, "mid": v(146.05, 216.25) * mm, "end": v(146.14, 216.39) * mm});
            skArc(sketch, "E293", {"start": v(146.14, 216.39) * mm, "mid": v(146.2, 216.51) * mm, "end": v(146.23, 216.65) * mm});
            skArc(sketch, "E294", {"start": v(146.23, 216.65) * mm, "mid": v(146.24, 216.74) * mm, "end": v(146.24, 216.83) * mm});
            skLineSegment(sketch, "E295", {"start": v(146.24, 216.83) * mm, "end": v(146.24, 217.8) * mm});
            skArc(sketch, "E296", {"start": v(146.24, 217.8) * mm, "mid": v(146.24, 217.94) * mm, "end": v(146.2, 218.07) * mm});
            skArc(sketch, "E297", {"start": v(146.2, 218.07) * mm, "mid": v(146.16, 218.2) * mm, "end": v(146.1, 218.33) * mm});
            skArc(sketch, "E298", {"start": v(146.1, 218.33) * mm, "mid": v(146, 218.47) * mm, "end": v(145.87, 218.6) * mm});
            skArc(sketch, "E299", {"start": v(145.87, 218.6) * mm, "mid": v(145.7, 218.73) * mm, "end": v(145.52, 218.84) * mm});
            skArc(sketch, "E300", {"start": v(145.52, 218.84) * mm, "mid": v(145.29, 218.93) * mm, "end": v(145.04, 219) * mm});
            skArc(sketch, "E301", {"start": v(145.04, 219) * mm, "mid": v(144.86, 219.02) * mm, "end": v(144.67, 219.03) * mm});
            skLineSegment(sketch, "E302", {"start": v(144.67, 219.03) * mm, "end": v(137.66, 219.03) * mm});
            skArc(sketch, "E303", {"start": v(137.66, 219.03) * mm, "mid": v(137.4, 219.01) * mm, "end": v(137.13, 218.96) * mm});
            skArc(sketch, "E304", {"start": v(137.13, 218.96) * mm, "mid": v(136.9, 218.88) * mm, "end": v(136.7, 218.77) * mm});
            skArc(sketch, "E305", {"start": v(136.7, 218.77) * mm, "mid": v(136.53, 218.66) * mm, "end": v(136.38, 218.52) * mm});
            skArc(sketch, "E306", {"start": v(136.38, 218.52) * mm, "mid": v(136.28, 218.4) * mm, "end": v(136.2, 218.25) * mm});
            skArc(sketch, "E307", {"start": v(136.2, 218.25) * mm, "mid": v(136.14, 218.13) * mm, "end": v(136.1, 218) * mm});
            skArc(sketch, "E308", {"start": v(136.1, 218) * mm, "mid": v(136.09, 217.9) * mm, "end": v(136.09, 217.8) * mm});
            skLineSegment(sketch, "E309", {"start": v(136.09, 198.94) * mm, "end": v(136.09, 197.96) * mm});
            skArc(sketch, "E310", {"start": v(136.09, 197.96) * mm, "mid": v(136.1, 197.83) * mm, "end": v(136.12, 197.7) * mm});
            skArc(sketch, "E311", {"start": v(136.12, 197.7) * mm, "mid": v(136.17, 197.56) * mm, "end": v(136.24, 197.43) * mm});
            skArc(sketch, "E312", {"start": v(136.24, 197.43) * mm, "mid": v(136.34, 197.3) * mm, "end": v(136.46, 197.17) * mm});
            skArc(sketch, "E313", {"start": v(136.46, 197.17) * mm, "mid": v(136.63, 197.04) * mm, "end": v(136.8, 196.93) * mm});
            skArc(sketch, "E314", {"start": v(136.8, 196.93) * mm, "mid": v(137.04, 196.83) * mm, "end": v(137.29, 196.77) * mm});
            skArc(sketch, "E315", {"start": v(137.29, 196.77) * mm, "mid": v(137.47, 196.75) * mm, "end": v(137.66, 196.74) * mm});
            skLineSegment(sketch, "E316", {"start": v(137.66, 196.74) * mm, "end": v(144.67, 196.74) * mm});
            skArc(sketch, "E317", {"start": v(144.67, 196.74) * mm, "mid": v(144.94, 196.75) * mm, "end": v(145.2, 196.8) * mm});
            skArc(sketch, "E318", {"start": v(145.2, 196.8) * mm, "mid": v(145.43, 196.89) * mm, "end": v(145.64, 197) * mm});
            skArc(sketch, "E319", {"start": v(145.64, 197) * mm, "mid": v(145.8, 197.11) * mm, "end": v(145.95, 197.25) * mm});
            skArc(sketch, "E320", {"start": v(145.95, 197.25) * mm, "mid": v(146.05, 197.37) * mm, "end": v(146.14, 197.51) * mm});
            skArc(sketch, "E321", {"start": v(146.14, 197.51) * mm, "mid": v(146.2, 197.64) * mm, "end": v(146.23, 197.77) * mm});
            skArc(sketch, "E322", {"start": v(146.23, 197.77) * mm, "mid": v(146.24, 197.87) * mm, "end": v(146.24, 197.96) * mm});
            skLineSegment(sketch, "E323", {"start": v(146.24, 197.96) * mm, "end": v(146.24, 198.94) * mm});
            skArc(sketch, "E324", {"start": v(146.24, 198.94) * mm, "mid": v(146.24, 199.07) * mm, "end": v(146.2, 199.2) * mm});
            skArc(sketch, "E325", {"start": v(146.2, 199.2) * mm, "mid": v(146.16, 199.33) * mm, "end": v(146.1, 199.46) * mm});
            skArc(sketch, "E326", {"start": v(146.1, 199.46) * mm, "mid": v(146, 199.6) * mm, "end": v(145.87, 199.72) * mm});
            skArc(sketch, "E327", {"start": v(145.87, 199.72) * mm, "mid": v(145.7, 199.86) * mm, "end": v(145.52, 199.96) * mm});
            skArc(sketch, "E328", {"start": v(145.52, 199.96) * mm, "mid": v(145.29, 200.06) * mm, "end": v(145.04, 200.12) * mm});
            skArc(sketch, "E329", {"start": v(145.04, 200.12) * mm, "mid": v(144.86, 200.15) * mm, "end": v(144.67, 200.16) * mm});
            skLineSegment(sketch, "E330", {"start": v(144.67, 200.16) * mm, "end": v(137.66, 200.16) * mm});
            skArc(sketch, "E331", {"start": v(137.66, 200.16) * mm, "mid": v(137.4, 200.14) * mm, "end": v(137.13, 200.09) * mm});
            skArc(sketch, "E332", {"start": v(137.13, 200.09) * mm, "mid": v(136.9, 200) * mm, "end": v(136.7, 199.9) * mm});
            skArc(sketch, "E333", {"start": v(136.7, 199.9) * mm, "mid": v(136.53, 199.78) * mm, "end": v(136.38, 199.65) * mm});
            skArc(sketch, "E334", {"start": v(136.38, 199.65) * mm, "mid": v(136.28, 199.52) * mm, "end": v(136.2, 199.38) * mm});
            skArc(sketch, "E335", {"start": v(136.2, 199.38) * mm, "mid": v(136.14, 199.25) * mm, "end": v(136.1, 199.12) * mm});
            skArc(sketch, "E336", {"start": v(136.1, 199.12) * mm, "mid": v(136.09, 199.03) * mm, "end": v(136.09, 198.94) * mm});
            skLineSegment(sketch, "E337", {"start": v(136.09, 205.23) * mm, "end": v(136.09, 204.25) * mm});
            skArc(sketch, "E338", {"start": v(136.09, 204.25) * mm, "mid": v(136.1, 204.12) * mm, "end": v(136.12, 203.99) * mm});
            skArc(sketch, "E339", {"start": v(136.12, 203.99) * mm, "mid": v(136.17, 203.85) * mm, "end": v(136.24, 203.72) * mm});
            skArc(sketch, "E340", {"start": v(136.24, 203.72) * mm, "mid": v(136.34, 203.58) * mm, "end": v(136.46, 203.46) * mm});
            skArc(sketch, "E341", {"start": v(136.46, 203.46) * mm, "mid": v(136.63, 203.33) * mm, "end": v(136.8, 203.22) * mm});
            skArc(sketch, "E342", {"start": v(136.8, 203.22) * mm, "mid": v(137.04, 203.12) * mm, "end": v(137.29, 203.06) * mm});
            skArc(sketch, "E343", {"start": v(137.29, 203.06) * mm, "mid": v(137.47, 203.04) * mm, "end": v(137.66, 203.03) * mm});
            skLineSegment(sketch, "E344", {"start": v(137.66, 203.03) * mm, "end": v(144.67, 203.03) * mm});
            skArc(sketch, "E345", {"start": v(144.67, 203.03) * mm, "mid": v(144.94, 203.05) * mm, "end": v(145.2, 203.1) * mm});
            skArc(sketch, "E346", {"start": v(145.2, 203.1) * mm, "mid": v(145.43, 203.18) * mm, "end": v(145.64, 203.29) * mm});
            skArc(sketch, "E347", {"start": v(145.64, 203.29) * mm, "mid": v(145.8, 203.4) * mm, "end": v(145.95, 203.54) * mm});
            skArc(sketch, "E348", {"start": v(145.95, 203.54) * mm, "mid": v(146.05, 203.66) * mm, "end": v(146.14, 203.8) * mm});
            skArc(sketch, "E349", {"start": v(146.14, 203.8) * mm, "mid": v(146.2, 203.93) * mm, "end": v(146.23, 204.06) * mm});
            skArc(sketch, "E350", {"start": v(146.23, 204.06) * mm, "mid": v(146.24, 204.16) * mm, "end": v(146.24, 204.25) * mm});
            skLineSegment(sketch, "E351", {"start": v(146.24, 204.25) * mm, "end": v(146.24, 205.23) * mm});
            skArc(sketch, "E352", {"start": v(146.24, 205.23) * mm, "mid": v(146.24, 205.36) * mm, "end": v(146.2, 205.49) * mm});
            skArc(sketch, "E353", {"start": v(146.2, 205.49) * mm, "mid": v(146.16, 205.62) * mm, "end": v(146.1, 205.75) * mm});
            skArc(sketch, "E354", {"start": v(146.1, 205.75) * mm, "mid": v(146, 205.9) * mm, "end": v(145.87, 206.02) * mm});
            skArc(sketch, "E355", {"start": v(145.87, 206.02) * mm, "mid": v(145.7, 206.15) * mm, "end": v(145.52, 206.25) * mm});
            skArc(sketch, "E356", {"start": v(145.52, 206.25) * mm, "mid": v(145.29, 206.35) * mm, "end": v(145.04, 206.41) * mm});
            skArc(sketch, "E357", {"start": v(145.04, 206.41) * mm, "mid": v(144.86, 206.44) * mm, "end": v(144.67, 206.45) * mm});
            skLineSegment(sketch, "E358", {"start": v(144.67, 206.45) * mm, "end": v(137.66, 206.45) * mm});
            skArc(sketch, "E359", {"start": v(137.66, 206.45) * mm, "mid": v(137.4, 206.43) * mm, "end": v(137.13, 206.38) * mm});
            skArc(sketch, "E360", {"start": v(137.13, 206.38) * mm, "mid": v(136.9, 206.3) * mm, "end": v(136.7, 206.19) * mm});
            skArc(sketch, "E361", {"start": v(136.7, 206.19) * mm, "mid": v(136.53, 206.07) * mm, "end": v(136.38, 205.94) * mm});
            skArc(sketch, "E362", {"start": v(136.38, 205.94) * mm, "mid": v(136.28, 205.81) * mm, "end": v(136.2, 205.67) * mm});
            skArc(sketch, "E363", {"start": v(136.2, 205.67) * mm, "mid": v(136.14, 205.54) * mm, "end": v(136.1, 205.41) * mm});
            skArc(sketch, "E364", {"start": v(136.1, 205.41) * mm, "mid": v(136.09, 205.32) * mm, "end": v(136.09, 205.23) * mm});
            skLineSegment(sketch, "E365", {"start": v(127.9, 186.84) * mm, "end": v(127.9, 170.6) * mm});
            skLineSegment(sketch, "E366", {"start": v(127.9, 170.6) * mm, "end": v(149.53, 170.6) * mm});
            skLineSegment(sketch, "E367", {"start": v(149.53, 170.6) * mm, "end": v(149.53, 186.84) * mm});
            skLineSegment(sketch, "E368", {"start": v(149.53, 186.84) * mm, "end": v(127.9, 186.84) * mm});
            skLineSegment(sketch, "E369", {"start": v(149.15, 164.85) * mm, "end": v(129.8, 164.85) * mm});
            skLineSegment(sketch, "E370", {"start": v(129.8, 164.85) * mm, "end": v(129.8, 102.08) * mm});
            skLineSegment(sketch, "E371", {"start": v(129.8, 102.08) * mm, "end": v(149.15, 102.08) * mm});
            skLineSegment(sketch, "E372", {"start": v(149.15, 102.08) * mm, "end": v(149.15, 164.85) * mm});
            skLineSegment(sketch, "E373", {"start": v(140.69, 159.4) * mm, "end": v(140.69, 107.2) * mm});
            skArc(sketch, "E374", {"start": v(140.69, 107.2) * mm, "mid": v(140.7, 106.92) * mm, "end": v(140.77, 106.64) * mm});
            skArc(sketch, "E375", {"start": v(140.77, 106.64) * mm, "mid": v(140.86, 106.39) * mm, "end": v(140.99, 106.14) * mm});
            skArc(sketch, "E376", {"start": v(140.99, 106.14) * mm, "mid": v(141.14, 105.92) * mm, "end": v(141.32, 105.73) * mm});
            skArc(sketch, "E377", {"start": v(141.32, 105.73) * mm, "mid": v(141.53, 105.56) * mm, "end": v(141.76, 105.43) * mm});
            skArc(sketch, "E378", {"start": v(141.76, 105.43) * mm, "mid": v(141.99, 105.33) * mm, "end": v(142.22, 105.27) * mm});
            skArc(sketch, "E379", {"start": v(142.22, 105.27) * mm, "mid": v(142.4, 105.24) * mm, "end": v(142.57, 105.23) * mm});
            skLineSegment(sketch, "E380", {"start": v(142.57, 105.23) * mm, "end": v(145.26, 105.23) * mm});
            skArc(sketch, "E381", {"start": v(145.26, 105.23) * mm, "mid": v(145.5, 105.25) * mm, "end": v(145.75, 105.3) * mm});
            skArc(sketch, "E382", {"start": v(145.75, 105.3) * mm, "mid": v(146, 105.4) * mm, "end": v(146.22, 105.51) * mm});
            skArc(sketch, "E383", {"start": v(146.22, 105.51) * mm, "mid": v(146.43, 105.67) * mm, "end": v(146.63, 105.86) * mm});
            skArc(sketch, "E384", {"start": v(146.63, 105.86) * mm, "mid": v(146.8, 106.07) * mm, "end": v(146.93, 106.3) * mm});
            skArc(sketch, "E385", {"start": v(146.93, 106.3) * mm, "mid": v(147.03, 106.56) * mm, "end": v(147.1, 106.83) * mm});
            skArc(sketch, "E386", {"start": v(147.1, 106.83) * mm, "mid": v(147.13, 107.02) * mm, "end": v(147.14, 107.2) * mm});
            skLineSegment(sketch, "E387", {"start": v(147.14, 107.2) * mm, "end": v(147.14, 159.4) * mm});
            skArc(sketch, "E388", {"start": v(147.14, 159.4) * mm, "mid": v(147.12, 159.7) * mm, "end": v(147.06, 159.97) * mm});
            skArc(sketch, "E389", {"start": v(147.06, 159.97) * mm, "mid": v(146.97, 160.23) * mm, "end": v(146.84, 160.47) * mm});
            skArc(sketch, "E390", {"start": v(146.84, 160.47) * mm, "mid": v(146.68, 160.69) * mm, "end": v(146.5, 160.88) * mm});
            skArc(sketch, "E391", {"start": v(146.5, 160.88) * mm, "mid": v(146.3, 161.05) * mm, "end": v(146.07, 161.19) * mm});
            skArc(sketch, "E392", {"start": v(146.07, 161.19) * mm, "mid": v(145.84, 161.28) * mm, "end": v(145.6, 161.35) * mm});
            skArc(sketch, "E393", {"start": v(145.6, 161.35) * mm, "mid": v(145.43, 161.37) * mm, "end": v(145.26, 161.38) * mm});
            skLineSegment(sketch, "E394", {"start": v(145.26, 161.38) * mm, "end": v(142.57, 161.38) * mm});
            skArc(sketch, "E395", {"start": v(142.57, 161.38) * mm, "mid": v(142.32, 161.36) * mm, "end": v(142.07, 161.3) * mm});
            skArc(sketch, "E396", {"start": v(142.07, 161.3) * mm, "mid": v(141.83, 161.22) * mm, "end": v(141.6, 161.1) * mm});
            skArc(sketch, "E397", {"start": v(141.6, 161.1) * mm, "mid": v(141.39, 160.94) * mm, "end": v(141.2, 160.76) * mm});
            skArc(sketch, "E398", {"start": v(141.2, 160.76) * mm, "mid": v(141.03, 160.55) * mm, "end": v(140.9, 160.31) * mm});
            skArc(sketch, "E399", {"start": v(140.9, 160.31) * mm, "mid": v(140.8, 160.06) * mm, "end": v(140.72, 159.79) * mm});
            skArc(sketch, "E400", {"start": v(140.72, 159.79) * mm, "mid": v(140.7, 159.6) * mm, "end": v(140.69, 159.4) * mm});
            skLineSegment(sketch, "E401", {"start": v(131.88, 159.56) * mm, "end": v(131.88, 107.36) * mm});
            skArc(sketch, "E402", {"start": v(131.88, 107.36) * mm, "mid": v(131.9, 107.08) * mm, "end": v(131.96, 106.8) * mm});
            skArc(sketch, "E403", {"start": v(131.96, 106.8) * mm, "mid": v(132.05, 106.54) * mm, "end": v(132.17, 106.3) * mm});
            skArc(sketch, "E404", {"start": v(132.17, 106.3) * mm, "mid": v(132.33, 106.08) * mm, "end": v(132.51, 105.88) * mm});
            skArc(sketch, "E405", {"start": v(132.51, 105.88) * mm, "mid": v(132.72, 105.72) * mm, "end": v(132.95, 105.58) * mm});
            skArc(sketch, "E406", {"start": v(132.95, 105.58) * mm, "mid": v(133.17, 105.49) * mm, "end": v(133.41, 105.42) * mm});
            skArc(sketch, "E407", {"start": v(133.41, 105.42) * mm, "mid": v(133.59, 105.4) * mm, "end": v(133.76, 105.39) * mm});
            skLineSegment(sketch, "E408", {"start": v(133.76, 105.39) * mm, "end": v(136.44, 105.39) * mm});
            skArc(sketch, "E409", {"start": v(136.44, 105.39) * mm, "mid": v(136.7, 105.4) * mm, "end": v(136.94, 105.46) * mm});
            skArc(sketch, "E410", {"start": v(136.94, 105.46) * mm, "mid": v(137.18, 105.55) * mm, "end": v(137.41, 105.67) * mm});
            skArc(sketch, "E411", {"start": v(137.41, 105.67) * mm, "mid": v(137.62, 105.83) * mm, "end": v(137.81, 106.01) * mm});
            skArc(sketch, "E412", {"start": v(137.81, 106.01) * mm, "mid": v(137.98, 106.22) * mm, "end": v(138.12, 106.46) * mm});
            skArc(sketch, "E413", {"start": v(138.12, 106.46) * mm, "mid": v(138.22, 106.71) * mm, "end": v(138.3, 106.98) * mm});
            skArc(sketch, "E414", {"start": v(138.3, 106.98) * mm, "mid": v(138.32, 107.17) * mm, "end": v(138.33, 107.36) * mm});
            skLineSegment(sketch, "E415", {"start": v(138.33, 107.36) * mm, "end": v(138.33, 159.56) * mm});
            skArc(sketch, "E416", {"start": v(138.33, 159.56) * mm, "mid": v(138.3, 159.85) * mm, "end": v(138.25, 160.13) * mm});
            skArc(sketch, "E417", {"start": v(138.25, 160.13) * mm, "mid": v(138.15, 160.38) * mm, "end": v(138.03, 160.63) * mm});
            skArc(sketch, "E418", {"start": v(138.03, 160.63) * mm, "mid": v(137.87, 160.84) * mm, "end": v(137.7, 161.04) * mm});
            skArc(sketch, "E419", {"start": v(137.7, 161.04) * mm, "mid": v(137.48, 161.2) * mm, "end": v(137.26, 161.34) * mm});
            skArc(sketch, "E420", {"start": v(137.26, 161.34) * mm, "mid": v(137.03, 161.44) * mm, "end": v(136.79, 161.5) * mm});
            skArc(sketch, "E421", {"start": v(136.79, 161.5) * mm, "mid": v(136.62, 161.53) * mm, "end": v(136.44, 161.53) * mm});
            skLineSegment(sketch, "E422", {"start": v(136.44, 161.53) * mm, "end": v(133.76, 161.53) * mm});
            skArc(sketch, "E423", {"start": v(133.76, 161.53) * mm, "mid": v(133.5, 161.52) * mm, "end": v(133.26, 161.46) * mm});
            skArc(sketch, "E424", {"start": v(133.26, 161.46) * mm, "mid": v(133.02, 161.38) * mm, "end": v(132.8, 161.25) * mm});
            skArc(sketch, "E425", {"start": v(132.8, 161.25) * mm, "mid": v(132.58, 161.1) * mm, "end": v(132.39, 160.91) * mm});
            skArc(sketch, "E426", {"start": v(132.39, 160.91) * mm, "mid": v(132.22, 160.7) * mm, "end": v(132.09, 160.47) * mm});
            skArc(sketch, "E427", {"start": v(132.09, 160.47) * mm, "mid": v(131.98, 160.21) * mm, "end": v(131.91, 159.94) * mm});
            skArc(sketch, "E428", {"start": v(131.91, 159.94) * mm, "mid": v(131.89, 159.75) * mm, "end": v(131.88, 159.56) * mm});
            skLineSegment(sketch, "E429", {"start": v(129.15, 96.17) * mm, "end": v(129.15, 91.54) * mm});
            skLineSegment(sketch, "E430", {"start": v(129.15, 91.54) * mm, "end": v(151.65, 91.54) * mm});
            skLineSegment(sketch, "E431", {"start": v(151.65, 91.54) * mm, "end": v(151.65, 96.17) * mm});
            skLineSegment(sketch, "E432", {"start": v(151.65, 96.17) * mm, "end": v(129.15, 96.17) * mm});
            skLineSegment(sketch, "E433", {"start": v(129.3, 77.79) * mm, "end": v(129.3, 73.16) * mm});
            skLineSegment(sketch, "E434", {"start": v(129.3, 73.16) * mm, "end": v(151.79, 73.16) * mm});
            skLineSegment(sketch, "E435", {"start": v(151.79, 73.16) * mm, "end": v(151.79, 77.79) * mm});
            skLineSegment(sketch, "E436", {"start": v(151.79, 77.79) * mm, "end": v(129.3, 77.79) * mm});
            skLineSegment(sketch, "E437", {"start": v(129.07, 63.66) * mm, "end": v(129.07, 38) * mm});
            skLineSegment(sketch, "E438", {"start": v(129.07, 38) * mm, "end": v(154.73, 38) * mm});
            skLineSegment(sketch, "E439", {"start": v(154.73, 38) * mm, "end": v(154.73, 63.66) * mm});
            skLineSegment(sketch, "E440", {"start": v(154.73, 63.66) * mm, "end": v(129.07, 63.66) * mm});
            skLineSegment(sketch, "E441", {"start": v(3.12, 192.94) * mm, "end": v(3.12, 47.35) * mm});
            skArc(sketch, "E442", {"start": v(3.12, 47.35) * mm, "mid": v(3.58, 46.24) * mm, "end": v(4.7, 45.78) * mm});
            skLineSegment(sketch, "E443", {"start": v(4.7, 45.78) * mm, "end": v(69.62, 45.78) * mm});
            skArc(sketch, "E444", {"start": v(69.62, 45.78) * mm, "mid": v(70.73, 46.24) * mm, "end": v(71.2, 47.35) * mm});
            skLineSegment(sketch, "E445", {"start": v(71.2, 47.35) * mm, "end": v(71.2, 192.94) * mm});
            skArc(sketch, "E446", {"start": v(71.2, 192.94) * mm, "mid": v(70.73, 194.05) * mm, "end": v(69.62, 194.51) * mm});
            skLineSegment(sketch, "E447", {"start": v(69.62, 194.51) * mm, "end": v(4.7, 194.51) * mm});
            skArc(sketch, "E448", {"start": v(4.7, 194.51) * mm, "mid": v(3.58, 194.05) * mm, "end": v(3.12, 192.94) * mm});
            skLineSegment(sketch, "E449", {"start": v(-111.1, 159.17) * mm, "end": v(-111.1, 106.97) * mm});
            skArc(sketch, "E450", {"start": v(-111.1, 106.97) * mm, "mid": v(-111.08, 106.68) * mm, "end": v(-111.02, 106.4) * mm});
            skArc(sketch, "E451", {"start": v(-111.02, 106.4) * mm, "mid": v(-110.92, 106.15) * mm, "end": v(-110.8, 105.9) * mm});
            skArc(sketch, "E452", {"start": v(-110.8, 105.9) * mm, "mid": v(-110.64, 105.69) * mm, "end": v(-110.46, 105.5) * mm});
            skArc(sketch, "E453", {"start": v(-110.46, 105.5) * mm, "mid": v(-110.25, 105.32) * mm, "end": v(-110.03, 105.19) * mm});
            skArc(sketch, "E454", {"start": v(-110.03, 105.19) * mm, "mid": v(-109.8, 105.1) * mm, "end": v(-109.56, 105.03) * mm});
            skArc(sketch, "E455", {"start": v(-109.56, 105.03) * mm, "mid": v(-109.39, 105) * mm, "end": v(-109.21, 105) * mm});
            skLineSegment(sketch, "E456", {"start": v(-109.21, 105) * mm, "end": v(-106.53, 105) * mm});
            skArc(sketch, "E457", {"start": v(-106.53, 105) * mm, "mid": v(-106.28, 105.01) * mm, "end": v(-106.03, 105.07) * mm});
            skArc(sketch, "E458", {"start": v(-106.03, 105.07) * mm, "mid": v(-105.79, 105.15) * mm, "end": v(-105.56, 105.27) * mm});
            skArc(sketch, "E459", {"start": v(-105.56, 105.27) * mm, "mid": v(-105.35, 105.43) * mm, "end": v(-105.16, 105.62) * mm});
            skArc(sketch, "E460", {"start": v(-105.16, 105.62) * mm, "mid": v(-105, 105.83) * mm, "end": v(-104.86, 106.06) * mm});
            skArc(sketch, "E461", {"start": v(-104.86, 106.06) * mm, "mid": v(-104.75, 106.32) * mm, "end": v(-104.68, 106.59) * mm});
            skArc(sketch, "E462", {"start": v(-104.68, 106.59) * mm, "mid": v(-104.66, 106.78) * mm, "end": v(-104.65, 106.97) * mm});
            skLineSegment(sketch, "E463", {"start": v(-104.65, 106.97) * mm, "end": v(-104.65, 159.17) * mm});
            skArc(sketch, "E464", {"start": v(-104.65, 159.17) * mm, "mid": v(-104.67, 159.45) * mm, "end": v(-104.72, 159.73) * mm});
            skArc(sketch, "E465", {"start": v(-104.72, 159.73) * mm, "mid": v(-104.82, 159.99) * mm, "end": v(-104.94, 160.23) * mm});
            skArc(sketch, "E466", {"start": v(-104.94, 160.23) * mm, "mid": v(-105.1, 160.45) * mm, "end": v(-105.28, 160.65) * mm});
            skArc(sketch, "E467", {"start": v(-105.28, 160.65) * mm, "mid": v(-105.49, 160.81) * mm, "end": v(-105.72, 160.95) * mm});
            skArc(sketch, "E468", {"start": v(-105.72, 160.95) * mm, "mid": v(-105.94, 161.04) * mm, "end": v(-106.18, 161.1) * mm});
            skArc(sketch, "E469", {"start": v(-106.18, 161.1) * mm, "mid": v(-106.35, 161.13) * mm, "end": v(-106.53, 161.14) * mm});
            skLineSegment(sketch, "E470", {"start": v(-106.53, 161.14) * mm, "end": v(-109.21, 161.14) * mm});
            skArc(sketch, "E471", {"start": v(-109.21, 161.14) * mm, "mid": v(-109.47, 161.12) * mm, "end": v(-109.71, 161.07) * mm});
            skArc(sketch, "E472", {"start": v(-109.71, 161.07) * mm, "mid": v(-109.95, 160.98) * mm, "end": v(-110.18, 160.86) * mm});
            skArc(sketch, "E473", {"start": v(-110.18, 160.86) * mm, "mid": v(-110.4, 160.7) * mm, "end": v(-110.58, 160.52) * mm});
            skArc(sketch, "E474", {"start": v(-110.58, 160.52) * mm, "mid": v(-110.75, 160.3) * mm, "end": v(-110.88, 160.07) * mm});
            skArc(sketch, "E475", {"start": v(-110.88, 160.07) * mm, "mid": v(-110.99, 159.82) * mm, "end": v(-111.06, 159.55) * mm});
            skArc(sketch, "E476", {"start": v(-111.06, 159.55) * mm, "mid": v(-111.09, 159.36) * mm, "end": v(-111.1, 159.17) * mm});
            skLineSegment(sketch, "E477", {"start": v(-119.9, 159.32) * mm, "end": v(-119.9, 107.12) * mm});
            skArc(sketch, "E478", {"start": v(-119.9, 107.12) * mm, "mid": v(-119.89, 106.84) * mm, "end": v(-119.83, 106.56) * mm});
            skArc(sketch, "E479", {"start": v(-119.83, 106.56) * mm, "mid": v(-119.73, 106.3) * mm, "end": v(-119.6, 106.06) * mm});
            skArc(sketch, "E480", {"start": v(-119.6, 106.06) * mm, "mid": v(-119.45, 105.84) * mm, "end": v(-119.27, 105.65) * mm});
            skArc(sketch, "E481", {"start": v(-119.27, 105.65) * mm, "mid": v(-119.06, 105.48) * mm, "end": v(-118.84, 105.34) * mm});
            skArc(sketch, "E482", {"start": v(-118.84, 105.34) * mm, "mid": v(-118.6, 105.25) * mm, "end": v(-118.37, 105.18) * mm});
            skArc(sketch, "E483", {"start": v(-118.37, 105.18) * mm, "mid": v(-118.2, 105.16) * mm, "end": v(-118.02, 105.15) * mm});
            skLineSegment(sketch, "E484", {"start": v(-118.02, 105.15) * mm, "end": v(-115.34, 105.15) * mm});
            skArc(sketch, "E485", {"start": v(-115.34, 105.15) * mm, "mid": v(-115.09, 105.17) * mm, "end": v(-114.84, 105.22) * mm});
            skArc(sketch, "E486", {"start": v(-114.84, 105.22) * mm, "mid": v(-114.6, 105.3) * mm, "end": v(-114.37, 105.43) * mm});
            skArc(sketch, "E487", {"start": v(-114.37, 105.43) * mm, "mid": v(-114.16, 105.59) * mm, "end": v(-113.97, 105.77) * mm});
            skArc(sketch, "E488", {"start": v(-113.97, 105.77) * mm, "mid": v(-113.8, 105.98) * mm, "end": v(-113.67, 106.22) * mm});
            skArc(sketch, "E489", {"start": v(-113.67, 106.22) * mm, "mid": v(-113.56, 106.47) * mm, "end": v(-113.5, 106.74) * mm});
            skArc(sketch, "E490", {"start": v(-113.5, 106.74) * mm, "mid": v(-113.47, 106.93) * mm, "end": v(-113.46, 107.12) * mm});
            skLineSegment(sketch, "E491", {"start": v(-113.46, 107.12) * mm, "end": v(-113.46, 159.32) * mm});
            skArc(sketch, "E492", {"start": v(-113.46, 159.32) * mm, "mid": v(-113.48, 159.6) * mm, "end": v(-113.53, 159.89) * mm});
            skArc(sketch, "E493", {"start": v(-113.53, 159.89) * mm, "mid": v(-113.63, 160.14) * mm, "end": v(-113.75, 160.39) * mm});
            skArc(sketch, "E494", {"start": v(-113.75, 160.39) * mm, "mid": v(-113.9, 160.6) * mm, "end": v(-114.1, 160.8) * mm});
            skArc(sketch, "E495", {"start": v(-114.1, 160.8) * mm, "mid": v(-114.3, 160.97) * mm, "end": v(-114.53, 161.1) * mm});
            skArc(sketch, "E496", {"start": v(-114.53, 161.1) * mm, "mid": v(-114.75, 161.2) * mm, "end": v(-115, 161.26) * mm});
            skArc(sketch, "E497", {"start": v(-115, 161.26) * mm, "mid": v(-115.16, 161.29) * mm, "end": v(-115.34, 161.3) * mm});
            skLineSegment(sketch, "E498", {"start": v(-115.34, 161.3) * mm, "end": v(-118.02, 161.3) * mm});
            skArc(sketch, "E499", {"start": v(-118.02, 161.3) * mm, "mid": v(-118.28, 161.28) * mm, "end": v(-118.52, 161.23) * mm});
            skArc(sketch, "E500", {"start": v(-118.52, 161.23) * mm, "mid": v(-118.76, 161.14) * mm, "end": v(-118.99, 161.02) * mm});
            skArc(sketch, "E501", {"start": v(-118.99, 161.02) * mm, "mid": v(-119.2, 160.86) * mm, "end": v(-119.4, 160.67) * mm});
            skArc(sketch, "E502", {"start": v(-119.4, 160.67) * mm, "mid": v(-119.56, 160.46) * mm, "end": v(-119.7, 160.23) * mm});
            skArc(sketch, "E503", {"start": v(-119.7, 160.23) * mm, "mid": v(-119.8, 159.97) * mm, "end": v(-119.87, 159.7) * mm});
            skArc(sketch, "E504", {"start": v(-119.87, 159.7) * mm, "mid": v(-119.9, 159.51) * mm, "end": v(-119.9, 159.32) * mm});
            skLineSegment(sketch, "E505", {"start": v(-126.5, 178.2) * mm, "end": v(-126.5, 172.44) * mm});
            skArc(sketch, "E506", {"start": v(-126.5, 172.44) * mm, "mid": v(-126.47, 172.16) * mm, "end": v(-126.41, 171.88) * mm});
            skArc(sketch, "E507", {"start": v(-126.41, 171.88) * mm, "mid": v(-126.32, 171.62) * mm, "end": v(-126.2, 171.38) * mm});
            skArc(sketch, "E508", {"start": v(-126.2, 171.38) * mm, "mid": v(-126.04, 171.16) * mm, "end": v(-125.86, 170.96) * mm});
            skArc(sketch, "E509", {"start": v(-125.86, 170.96) * mm, "mid": v(-125.65, 170.8) * mm, "end": v(-125.42, 170.66) * mm});
            skArc(sketch, "E510", {"start": v(-125.42, 170.66) * mm, "mid": v(-125.2, 170.56) * mm, "end": v(-124.95, 170.5) * mm});
            skArc(sketch, "E511", {"start": v(-124.95, 170.5) * mm, "mid": v(-124.78, 170.48) * mm, "end": v(-124.6, 170.47) * mm});
            skLineSegment(sketch, "E512", {"start": v(-124.6, 170.47) * mm, "end": v(-104.51, 170.47) * mm});
            skArc(sketch, "E513", {"start": v(-104.51, 170.47) * mm, "mid": v(-104.26, 170.49) * mm, "end": v(-104.02, 170.54) * mm});
            skArc(sketch, "E514", {"start": v(-104.02, 170.54) * mm, "mid": v(-103.77, 170.63) * mm, "end": v(-103.55, 170.75) * mm});
            skArc(sketch, "E515", {"start": v(-103.55, 170.75) * mm, "mid": v(-103.33, 170.9) * mm, "end": v(-103.14, 171.09) * mm});
            skArc(sketch, "E516", {"start": v(-103.14, 171.09) * mm, "mid": v(-102.98, 171.3) * mm, "end": v(-102.84, 171.53) * mm});
            skArc(sketch, "E517", {"start": v(-102.84, 171.53) * mm, "mid": v(-102.74, 171.8) * mm, "end": v(-102.67, 172.06) * mm});
            skArc(sketch, "E518", {"start": v(-102.67, 172.06) * mm, "mid": v(-102.64, 172.25) * mm, "end": v(-102.63, 172.44) * mm});
            skLineSegment(sketch, "E519", {"start": v(-102.63, 172.44) * mm, "end": v(-102.63, 178.2) * mm});
            skArc(sketch, "E520", {"start": v(-102.63, 178.2) * mm, "mid": v(-102.65, 178.48) * mm, "end": v(-102.71, 178.75) * mm});
            skArc(sketch, "E521", {"start": v(-102.71, 178.75) * mm, "mid": v(-102.8, 179.01) * mm, "end": v(-102.93, 179.26) * mm});
            skArc(sketch, "E522", {"start": v(-102.93, 179.26) * mm, "mid": v(-103.09, 179.47) * mm, "end": v(-103.27, 179.67) * mm});
            skArc(sketch, "E523", {"start": v(-103.27, 179.67) * mm, "mid": v(-103.48, 179.84) * mm, "end": v(-103.7, 179.97) * mm});
            skArc(sketch, "E524", {"start": v(-103.7, 179.97) * mm, "mid": v(-103.93, 180.07) * mm, "end": v(-104.17, 180.13) * mm});
            skArc(sketch, "E525", {"start": v(-104.17, 180.13) * mm, "mid": v(-104.34, 180.16) * mm, "end": v(-104.51, 180.16) * mm});
            skLineSegment(sketch, "E526", {"start": v(-104.51, 180.16) * mm, "end": v(-124.6, 180.16) * mm});
            skArc(sketch, "E527", {"start": v(-124.6, 180.16) * mm, "mid": v(-124.86, 180.15) * mm, "end": v(-125.1, 180.1) * mm});
            skArc(sketch, "E528", {"start": v(-125.1, 180.1) * mm, "mid": v(-125.35, 180) * mm, "end": v(-125.58, 179.88) * mm});
            skArc(sketch, "E529", {"start": v(-125.58, 179.88) * mm, "mid": v(-125.79, 179.73) * mm, "end": v(-125.98, 179.54) * mm});
            skArc(sketch, "E530", {"start": v(-125.98, 179.54) * mm, "mid": v(-126.15, 179.33) * mm, "end": v(-126.28, 179.1) * mm});
            skArc(sketch, "E531", {"start": v(-126.28, 179.1) * mm, "mid": v(-126.39, 178.84) * mm, "end": v(-126.46, 178.57) * mm});
            skArc(sketch, "E532", {"start": v(-126.46, 178.57) * mm, "mid": v(-126.48, 178.38) * mm, "end": v(-126.5, 178.2) * mm});
            skLineSegment(sketch, "E533", {"start": v(-126.5, 193.75) * mm, "end": v(-126.5, 188) * mm});
            skArc(sketch, "E534", {"start": v(-126.5, 188) * mm, "mid": v(-126.47, 187.72) * mm, "end": v(-126.41, 187.44) * mm});
            skArc(sketch, "E535", {"start": v(-126.41, 187.44) * mm, "mid": v(-126.32, 187.18) * mm, "end": v(-126.2, 186.94) * mm});
            skArc(sketch, "E536", {"start": v(-126.2, 186.94) * mm, "mid": v(-126.04, 186.72) * mm, "end": v(-125.86, 186.52) * mm});
            skArc(sketch, "E537", {"start": v(-125.86, 186.52) * mm, "mid": v(-125.65, 186.36) * mm, "end": v(-125.42, 186.22) * mm});
            skArc(sketch, "E538", {"start": v(-125.42, 186.22) * mm, "mid": v(-125.2, 186.12) * mm, "end": v(-124.95, 186.06) * mm});
            skArc(sketch, "E539", {"start": v(-124.95, 186.06) * mm, "mid": v(-124.78, 186.04) * mm, "end": v(-124.6, 186.03) * mm});
            skLineSegment(sketch, "E540", {"start": v(-124.6, 186.03) * mm, "end": v(-104.51, 186.03) * mm});
            skArc(sketch, "E541", {"start": v(-104.51, 186.03) * mm, "mid": v(-104.26, 186.04) * mm, "end": v(-104.02, 186.1) * mm});
            skArc(sketch, "E542", {"start": v(-104.02, 186.1) * mm, "mid": v(-103.77, 186.19) * mm, "end": v(-103.55, 186.3) * mm});
            skArc(sketch, "E543", {"start": v(-103.55, 186.3) * mm, "mid": v(-103.33, 186.46) * mm, "end": v(-103.14, 186.65) * mm});
            skArc(sketch, "E544", {"start": v(-103.14, 186.65) * mm, "mid": v(-102.98, 186.86) * mm, "end": v(-102.84, 187.1) * mm});
            skArc(sketch, "E545", {"start": v(-102.84, 187.1) * mm, "mid": v(-102.74, 187.35) * mm, "end": v(-102.67, 187.62) * mm});
            skArc(sketch, "E546", {"start": v(-102.67, 187.62) * mm, "mid": v(-102.64, 187.8) * mm, "end": v(-102.63, 188) * mm});
            skLineSegment(sketch, "E547", {"start": v(-102.63, 188) * mm, "end": v(-102.63, 193.75) * mm});
            skArc(sketch, "E548", {"start": v(-102.63, 193.75) * mm, "mid": v(-102.65, 194.03) * mm, "end": v(-102.71, 194.31) * mm});
            skArc(sketch, "E549", {"start": v(-102.71, 194.31) * mm, "mid": v(-102.8, 194.57) * mm, "end": v(-102.93, 194.81) * mm});
            skArc(sketch, "E550", {"start": v(-102.93, 194.81) * mm, "mid": v(-103.09, 195.03) * mm, "end": v(-103.27, 195.23) * mm});
            skArc(sketch, "E551", {"start": v(-103.27, 195.23) * mm, "mid": v(-103.48, 195.4) * mm, "end": v(-103.7, 195.53) * mm});
            skArc(sketch, "E552", {"start": v(-103.7, 195.53) * mm, "mid": v(-103.93, 195.63) * mm, "end": v(-104.17, 195.7) * mm});
            skArc(sketch, "E553", {"start": v(-104.17, 195.7) * mm, "mid": v(-104.34, 195.72) * mm, "end": v(-104.51, 195.72) * mm});
            skLineSegment(sketch, "E554", {"start": v(-104.51, 195.72) * mm, "end": v(-124.6, 195.72) * mm});
            skArc(sketch, "E555", {"start": v(-124.6, 195.72) * mm, "mid": v(-124.86, 195.7) * mm, "end": v(-125.1, 195.65) * mm});
            skArc(sketch, "E556", {"start": v(-125.1, 195.65) * mm, "mid": v(-125.35, 195.56) * mm, "end": v(-125.58, 195.44) * mm});
            skArc(sketch, "E557", {"start": v(-125.58, 195.44) * mm, "mid": v(-125.79, 195.29) * mm, "end": v(-125.98, 195.1) * mm});
            skArc(sketch, "E558", {"start": v(-125.98, 195.1) * mm, "mid": v(-126.15, 194.89) * mm, "end": v(-126.28, 194.66) * mm});
            skArc(sketch, "E559", {"start": v(-126.28, 194.66) * mm, "mid": v(-126.39, 194.4) * mm, "end": v(-126.46, 194.13) * mm});
            skArc(sketch, "E560", {"start": v(-126.46, 194.13) * mm, "mid": v(-126.48, 193.94) * mm, "end": v(-126.5, 193.75) * mm});
            skLineSegment(sketch, "E561", {"start": v(-83.44, 184.18) * mm, "end": v(-83.44, 183.2) * mm});
            skArc(sketch, "E562", {"start": v(-83.44, 183.2) * mm, "mid": v(-83.43, 183.07) * mm, "end": v(-83.4, 182.94) * mm});
            skArc(sketch, "E563", {"start": v(-83.4, 182.94) * mm, "mid": v(-83.35, 182.8) * mm, "end": v(-83.28, 182.68) * mm});
            skArc(sketch, "E564", {"start": v(-83.28, 182.68) * mm, "mid": v(-83.18, 182.54) * mm, "end": v(-83.06, 182.41) * mm});
            skArc(sketch, "E565", {"start": v(-83.06, 182.41) * mm, "mid": v(-82.9, 182.28) * mm, "end": v(-82.71, 182.17) * mm});
            skArc(sketch, "E566", {"start": v(-82.71, 182.17) * mm, "mid": v(-82.48, 182.08) * mm, "end": v(-82.23, 182.01) * mm});
            skArc(sketch, "E567", {"start": v(-82.23, 182.01) * mm, "mid": v(-82.05, 181.99) * mm, "end": v(-81.86, 181.98) * mm});
            skLineSegment(sketch, "E568", {"start": v(-81.86, 181.98) * mm, "end": v(-74.85, 181.98) * mm});
            skArc(sketch, "E569", {"start": v(-74.85, 181.98) * mm, "mid": v(-74.58, 182) * mm, "end": v(-74.32, 182.05) * mm});
            skArc(sketch, "E570", {"start": v(-74.32, 182.05) * mm, "mid": v(-74.1, 182.13) * mm, "end": v(-73.88, 182.24) * mm});
            skArc(sketch, "E571", {"start": v(-73.88, 182.24) * mm, "mid": v(-73.72, 182.35) * mm, "end": v(-73.57, 182.5) * mm});
            skArc(sketch, "E572", {"start": v(-73.57, 182.5) * mm, "mid": v(-73.47, 182.62) * mm, "end": v(-73.38, 182.76) * mm});
            skArc(sketch, "E573", {"start": v(-73.38, 182.76) * mm, "mid": v(-73.33, 182.88) * mm, "end": v(-73.3, 183.02) * mm});
            skArc(sketch, "E574", {"start": v(-73.3, 183.02) * mm, "mid": v(-73.28, 183.1) * mm, "end": v(-73.28, 183.2) * mm});
            skLineSegment(sketch, "E575", {"start": v(-73.28, 183.2) * mm, "end": v(-73.28, 184.18) * mm});
            skArc(sketch, "E576", {"start": v(-73.28, 184.18) * mm, "mid": v(-73.29, 184.31) * mm, "end": v(-73.31, 184.44) * mm});
            skArc(sketch, "E577", {"start": v(-73.31, 184.44) * mm, "mid": v(-73.36, 184.58) * mm, "end": v(-73.43, 184.7) * mm});
            skArc(sketch, "E578", {"start": v(-73.43, 184.7) * mm, "mid": v(-73.53, 184.85) * mm, "end": v(-73.65, 184.97) * mm});
            skArc(sketch, "E579", {"start": v(-73.65, 184.97) * mm, "mid": v(-73.82, 185.1) * mm, "end": v(-74, 185.2) * mm});
            skArc(sketch, "E580", {"start": v(-74, 185.2) * mm, "mid": v(-74.24, 185.3) * mm, "end": v(-74.48, 185.37) * mm});
            skArc(sketch, "E581", {"start": v(-74.48, 185.37) * mm, "mid": v(-74.66, 185.4) * mm, "end": v(-74.85, 185.4) * mm});
            skLineSegment(sketch, "E582", {"start": v(-74.85, 185.4) * mm, "end": v(-81.86, 185.4) * mm});
            skArc(sketch, "E583", {"start": v(-81.86, 185.4) * mm, "mid": v(-82.13, 185.38) * mm, "end": v(-82.4, 185.33) * mm});
            skArc(sketch, "E584", {"start": v(-82.4, 185.33) * mm, "mid": v(-82.62, 185.25) * mm, "end": v(-82.83, 185.14) * mm});
            skArc(sketch, "E585", {"start": v(-82.83, 185.14) * mm, "mid": v(-83, 185.03) * mm, "end": v(-83.14, 184.89) * mm});
            skArc(sketch, "E586", {"start": v(-83.14, 184.89) * mm, "mid": v(-83.25, 184.76) * mm, "end": v(-83.33, 184.62) * mm});
            skArc(sketch, "E587", {"start": v(-83.33, 184.62) * mm, "mid": v(-83.38, 184.5) * mm, "end": v(-83.42, 184.36) * mm});
            skArc(sketch, "E588", {"start": v(-83.42, 184.36) * mm, "mid": v(-83.43, 184.27) * mm, "end": v(-83.44, 184.18) * mm});
            skLineSegment(sketch, "E589", {"start": v(-83.44, 177.89) * mm, "end": v(-83.44, 176.91) * mm});
            skArc(sketch, "E590", {"start": v(-83.44, 176.91) * mm, "mid": v(-83.43, 176.78) * mm, "end": v(-83.4, 176.65) * mm});
            skArc(sketch, "E591", {"start": v(-83.4, 176.65) * mm, "mid": v(-83.35, 176.51) * mm, "end": v(-83.28, 176.38) * mm});
            skArc(sketch, "E592", {"start": v(-83.28, 176.38) * mm, "mid": v(-83.18, 176.25) * mm, "end": v(-83.06, 176.12) * mm});
            skArc(sketch, "E593", {"start": v(-83.06, 176.12) * mm, "mid": v(-82.9, 176) * mm, "end": v(-82.71, 175.88) * mm});
            skArc(sketch, "E594", {"start": v(-82.71, 175.88) * mm, "mid": v(-82.48, 175.79) * mm, "end": v(-82.23, 175.72) * mm});
            skArc(sketch, "E595", {"start": v(-82.23, 175.72) * mm, "mid": v(-82.05, 175.7) * mm, "end": v(-81.86, 175.7) * mm});
            skLineSegment(sketch, "E596", {"start": v(-81.86, 175.7) * mm, "end": v(-74.85, 175.7) * mm});
            skArc(sketch, "E597", {"start": v(-74.85, 175.7) * mm, "mid": v(-74.58, 175.7) * mm, "end": v(-74.32, 175.76) * mm});
            skArc(sketch, "E598", {"start": v(-74.32, 175.76) * mm, "mid": v(-74.1, 175.84) * mm, "end": v(-73.88, 175.95) * mm});
            skArc(sketch, "E599", {"start": v(-73.88, 175.95) * mm, "mid": v(-73.72, 176.06) * mm, "end": v(-73.57, 176.2) * mm});
            skArc(sketch, "E600", {"start": v(-73.57, 176.2) * mm, "mid": v(-73.47, 176.33) * mm, "end": v(-73.38, 176.47) * mm});
            skArc(sketch, "E601", {"start": v(-73.38, 176.47) * mm, "mid": v(-73.33, 176.6) * mm, "end": v(-73.3, 176.73) * mm});
            skArc(sketch, "E602", {"start": v(-73.3, 176.73) * mm, "mid": v(-73.28, 176.82) * mm, "end": v(-73.28, 176.91) * mm});
            skLineSegment(sketch, "E603", {"start": v(-73.28, 176.91) * mm, "end": v(-73.28, 177.89) * mm});
            skArc(sketch, "E604", {"start": v(-73.28, 177.89) * mm, "mid": v(-73.29, 178.02) * mm, "end": v(-73.31, 178.15) * mm});
            skArc(sketch, "E605", {"start": v(-73.31, 178.15) * mm, "mid": v(-73.36, 178.29) * mm, "end": v(-73.43, 178.42) * mm});
            skArc(sketch, "E606", {"start": v(-73.43, 178.42) * mm, "mid": v(-73.53, 178.55) * mm, "end": v(-73.65, 178.68) * mm});
            skArc(sketch, "E607", {"start": v(-73.65, 178.68) * mm, "mid": v(-73.82, 178.8) * mm, "end": v(-74, 178.92) * mm});
            skArc(sketch, "E608", {"start": v(-74, 178.92) * mm, "mid": v(-74.24, 179.01) * mm, "end": v(-74.48, 179.08) * mm});
            skArc(sketch, "E609", {"start": v(-74.48, 179.08) * mm, "mid": v(-74.66, 179.1) * mm, "end": v(-74.85, 179.1) * mm});
            skLineSegment(sketch, "E610", {"start": v(-74.85, 179.1) * mm, "end": v(-81.86, 179.1) * mm});
            skArc(sketch, "E611", {"start": v(-81.86, 179.1) * mm, "mid": v(-82.13, 179.1) * mm, "end": v(-82.4, 179.04) * mm});
            skArc(sketch, "E612", {"start": v(-82.4, 179.04) * mm, "mid": v(-82.62, 178.96) * mm, "end": v(-82.83, 178.85) * mm});
            skArc(sketch, "E613", {"start": v(-82.83, 178.85) * mm, "mid": v(-83, 178.74) * mm, "end": v(-83.14, 178.6) * mm});
            skArc(sketch, "E614", {"start": v(-83.14, 178.6) * mm, "mid": v(-83.25, 178.47) * mm, "end": v(-83.33, 178.33) * mm});
            skArc(sketch, "E615", {"start": v(-83.33, 178.33) * mm, "mid": v(-83.38, 178.2) * mm, "end": v(-83.42, 178.07) * mm});
            skArc(sketch, "E616", {"start": v(-83.42, 178.07) * mm, "mid": v(-83.43, 177.98) * mm, "end": v(-83.44, 177.89) * mm});
            skLineSegment(sketch, "E617", {"start": v(-83.44, 165.3) * mm, "end": v(-83.44, 164.33) * mm});
            skArc(sketch, "E618", {"start": v(-83.44, 164.33) * mm, "mid": v(-83.43, 164.2) * mm, "end": v(-83.4, 164.07) * mm});
            skArc(sketch, "E619", {"start": v(-83.4, 164.07) * mm, "mid": v(-83.35, 163.93) * mm, "end": v(-83.28, 163.8) * mm});
            skArc(sketch, "E620", {"start": v(-83.28, 163.8) * mm, "mid": v(-83.18, 163.66) * mm, "end": v(-83.06, 163.54) * mm});
            skArc(sketch, "E621", {"start": v(-83.06, 163.54) * mm, "mid": v(-82.9, 163.4) * mm, "end": v(-82.71, 163.3) * mm});
            skArc(sketch, "E622", {"start": v(-82.71, 163.3) * mm, "mid": v(-82.48, 163.2) * mm, "end": v(-82.23, 163.14) * mm});
            skArc(sketch, "E623", {"start": v(-82.23, 163.14) * mm, "mid": v(-82.05, 163.12) * mm, "end": v(-81.86, 163.1) * mm});
            skLineSegment(sketch, "E624", {"start": v(-81.86, 163.1) * mm, "end": v(-74.85, 163.1) * mm});
            skArc(sketch, "E625", {"start": v(-74.85, 163.1) * mm, "mid": v(-74.58, 163.13) * mm, "end": v(-74.32, 163.18) * mm});
            skArc(sketch, "E626", {"start": v(-74.32, 163.18) * mm, "mid": v(-74.1, 163.26) * mm, "end": v(-73.88, 163.37) * mm});
            skArc(sketch, "E627", {"start": v(-73.88, 163.37) * mm, "mid": v(-73.72, 163.48) * mm, "end": v(-73.57, 163.62) * mm});
            skArc(sketch, "E628", {"start": v(-73.57, 163.62) * mm, "mid": v(-73.47, 163.75) * mm, "end": v(-73.38, 163.88) * mm});
            skArc(sketch, "E629", {"start": v(-73.38, 163.88) * mm, "mid": v(-73.33, 164.01) * mm, "end": v(-73.3, 164.14) * mm});
            skArc(sketch, "E630", {"start": v(-73.3, 164.14) * mm, "mid": v(-73.28, 164.24) * mm, "end": v(-73.28, 164.33) * mm});
            skLineSegment(sketch, "E631", {"start": v(-73.28, 164.33) * mm, "end": v(-73.28, 165.3) * mm});
            skArc(sketch, "E632", {"start": v(-73.28, 165.3) * mm, "mid": v(-73.29, 165.44) * mm, "end": v(-73.31, 165.57) * mm});
            skArc(sketch, "E633", {"start": v(-73.31, 165.57) * mm, "mid": v(-73.36, 165.7) * mm, "end": v(-73.43, 165.83) * mm});
            skArc(sketch, "E634", {"start": v(-73.43, 165.83) * mm, "mid": v(-73.53, 165.97) * mm, "end": v(-73.65, 166.1) * mm});
            skArc(sketch, "E635", {"start": v(-73.65, 166.1) * mm, "mid": v(-73.82, 166.23) * mm, "end": v(-74, 166.33) * mm});
            skArc(sketch, "E636", {"start": v(-74, 166.33) * mm, "mid": v(-74.24, 166.43) * mm, "end": v(-74.48, 166.5) * mm});
            skArc(sketch, "E637", {"start": v(-74.48, 166.5) * mm, "mid": v(-74.66, 166.52) * mm, "end": v(-74.85, 166.53) * mm});
            skLineSegment(sketch, "E638", {"start": v(-74.85, 166.53) * mm, "end": v(-81.86, 166.53) * mm});
            skArc(sketch, "E639", {"start": v(-81.86, 166.53) * mm, "mid": v(-82.13, 166.51) * mm, "end": v(-82.4, 166.46) * mm});
            skArc(sketch, "E640", {"start": v(-82.4, 166.46) * mm, "mid": v(-82.62, 166.38) * mm, "end": v(-82.83, 166.27) * mm});
            skArc(sketch, "E641", {"start": v(-82.83, 166.27) * mm, "mid": v(-83, 166.15) * mm, "end": v(-83.14, 166.02) * mm});
            skArc(sketch, "E642", {"start": v(-83.14, 166.02) * mm, "mid": v(-83.25, 165.9) * mm, "end": v(-83.33, 165.75) * mm});
            skArc(sketch, "E643", {"start": v(-83.33, 165.75) * mm, "mid": v(-83.38, 165.63) * mm, "end": v(-83.42, 165.5) * mm});
            skArc(sketch, "E644", {"start": v(-83.42, 165.5) * mm, "mid": v(-83.43, 165.4) * mm, "end": v(-83.44, 165.3) * mm});
            skLineSegment(sketch, "E645", {"start": v(-83.44, 171.6) * mm, "end": v(-83.44, 170.62) * mm});
            skArc(sketch, "E646", {"start": v(-83.44, 170.62) * mm, "mid": v(-83.43, 170.49) * mm, "end": v(-83.4, 170.36) * mm});
            skArc(sketch, "E647", {"start": v(-83.4, 170.36) * mm, "mid": v(-83.35, 170.22) * mm, "end": v(-83.28, 170.1) * mm});
            skArc(sketch, "E648", {"start": v(-83.28, 170.1) * mm, "mid": v(-83.18, 169.95) * mm, "end": v(-83.06, 169.83) * mm});
            skArc(sketch, "E649", {"start": v(-83.06, 169.83) * mm, "mid": v(-82.9, 169.7) * mm, "end": v(-82.71, 169.6) * mm});
            skArc(sketch, "E650", {"start": v(-82.71, 169.6) * mm, "mid": v(-82.48, 169.5) * mm, "end": v(-82.23, 169.43) * mm});
            skArc(sketch, "E651", {"start": v(-82.23, 169.43) * mm, "mid": v(-82.05, 169.4) * mm, "end": v(-81.86, 169.4) * mm});
            skLineSegment(sketch, "E652", {"start": v(-81.86, 169.4) * mm, "end": v(-74.85, 169.4) * mm});
            skArc(sketch, "E653", {"start": v(-74.85, 169.4) * mm, "mid": v(-74.58, 169.42) * mm, "end": v(-74.32, 169.47) * mm});
            skArc(sketch, "E654", {"start": v(-74.32, 169.47) * mm, "mid": v(-74.1, 169.55) * mm, "end": v(-73.88, 169.66) * mm});
            skArc(sketch, "E655", {"start": v(-73.88, 169.66) * mm, "mid": v(-73.72, 169.77) * mm, "end": v(-73.57, 169.9) * mm});
            skArc(sketch, "E656", {"start": v(-73.57, 169.9) * mm, "mid": v(-73.47, 170.04) * mm, "end": v(-73.38, 170.18) * mm});
            skArc(sketch, "E657", {"start": v(-73.38, 170.18) * mm, "mid": v(-73.33, 170.3) * mm, "end": v(-73.3, 170.44) * mm});
            skArc(sketch, "E658", {"start": v(-73.3, 170.44) * mm, "mid": v(-73.28, 170.53) * mm, "end": v(-73.28, 170.62) * mm});
            skLineSegment(sketch, "E659", {"start": v(-73.28, 170.62) * mm, "end": v(-73.28, 171.6) * mm});
            skArc(sketch, "E660", {"start": v(-73.28, 171.6) * mm, "mid": v(-73.29, 171.73) * mm, "end": v(-73.31, 171.86) * mm});
            skArc(sketch, "E661", {"start": v(-73.31, 171.86) * mm, "mid": v(-73.36, 172) * mm, "end": v(-73.43, 172.12) * mm});
            skArc(sketch, "E662", {"start": v(-73.43, 172.12) * mm, "mid": v(-73.53, 172.26) * mm, "end": v(-73.65, 172.39) * mm});
            skArc(sketch, "E663", {"start": v(-73.65, 172.39) * mm, "mid": v(-73.82, 172.52) * mm, "end": v(-74, 172.63) * mm});
            skArc(sketch, "E664", {"start": v(-74, 172.63) * mm, "mid": v(-74.24, 172.72) * mm, "end": v(-74.48, 172.78) * mm});
            skArc(sketch, "E665", {"start": v(-74.48, 172.78) * mm, "mid": v(-74.66, 172.81) * mm, "end": v(-74.85, 172.82) * mm});
            skLineSegment(sketch, "E666", {"start": v(-74.85, 172.82) * mm, "end": v(-81.86, 172.82) * mm});
            skArc(sketch, "E667", {"start": v(-81.86, 172.82) * mm, "mid": v(-82.13, 172.8) * mm, "end": v(-82.4, 172.75) * mm});
            skArc(sketch, "E668", {"start": v(-82.4, 172.75) * mm, "mid": v(-82.62, 172.67) * mm, "end": v(-82.83, 172.56) * mm});
            skArc(sketch, "E669", {"start": v(-82.83, 172.56) * mm, "mid": v(-83, 172.45) * mm, "end": v(-83.14, 172.3) * mm});
            skArc(sketch, "E670", {"start": v(-83.14, 172.3) * mm, "mid": v(-83.25, 172.18) * mm, "end": v(-83.33, 172.04) * mm});
            skArc(sketch, "E671", {"start": v(-83.33, 172.04) * mm, "mid": v(-83.38, 171.92) * mm, "end": v(-83.42, 171.78) * mm});
            skArc(sketch, "E672", {"start": v(-83.42, 171.78) * mm, "mid": v(-83.43, 171.7) * mm, "end": v(-83.44, 171.6) * mm});
            skLineSegment(sketch, "E673", {"start": v(-83.44, 152.73) * mm, "end": v(-83.44, 151.75) * mm});
            skArc(sketch, "E674", {"start": v(-83.44, 151.75) * mm, "mid": v(-83.43, 151.62) * mm, "end": v(-83.4, 151.49) * mm});
            skArc(sketch, "E675", {"start": v(-83.4, 151.49) * mm, "mid": v(-83.35, 151.35) * mm, "end": v(-83.28, 151.22) * mm});
            skArc(sketch, "E676", {"start": v(-83.28, 151.22) * mm, "mid": v(-83.18, 151.08) * mm, "end": v(-83.06, 150.96) * mm});
            skArc(sketch, "E677", {"start": v(-83.06, 150.96) * mm, "mid": v(-82.9, 150.83) * mm, "end": v(-82.71, 150.72) * mm});
            skArc(sketch, "E678", {"start": v(-82.71, 150.72) * mm, "mid": v(-82.48, 150.62) * mm, "end": v(-82.23, 150.56) * mm});
            skArc(sketch, "E679", {"start": v(-82.23, 150.56) * mm, "mid": v(-82.05, 150.54) * mm, "end": v(-81.86, 150.53) * mm});
            skLineSegment(sketch, "E680", {"start": v(-81.86, 150.53) * mm, "end": v(-74.85, 150.53) * mm});
            skArc(sketch, "E681", {"start": v(-74.85, 150.53) * mm, "mid": v(-74.58, 150.54) * mm, "end": v(-74.32, 150.6) * mm});
            skArc(sketch, "E682", {"start": v(-74.32, 150.6) * mm, "mid": v(-74.1, 150.68) * mm, "end": v(-73.88, 150.79) * mm});
            skArc(sketch, "E683", {"start": v(-73.88, 150.79) * mm, "mid": v(-73.72, 150.9) * mm, "end": v(-73.57, 151.04) * mm});
            skArc(sketch, "E684", {"start": v(-73.57, 151.04) * mm, "mid": v(-73.47, 151.16) * mm, "end": v(-73.38, 151.3) * mm});
            skArc(sketch, "E685", {"start": v(-73.38, 151.3) * mm, "mid": v(-73.33, 151.43) * mm, "end": v(-73.3, 151.56) * mm});
            skArc(sketch, "E686", {"start": v(-73.3, 151.56) * mm, "mid": v(-73.28, 151.66) * mm, "end": v(-73.28, 151.75) * mm});
            skLineSegment(sketch, "E687", {"start": v(-73.28, 151.75) * mm, "end": v(-73.28, 152.73) * mm});
            skArc(sketch, "E688", {"start": v(-73.28, 152.73) * mm, "mid": v(-73.29, 152.86) * mm, "end": v(-73.31, 152.99) * mm});
            skArc(sketch, "E689", {"start": v(-73.31, 152.99) * mm, "mid": v(-73.36, 153.12) * mm, "end": v(-73.43, 153.25) * mm});
            skArc(sketch, "E690", {"start": v(-73.43, 153.25) * mm, "mid": v(-73.53, 153.4) * mm, "end": v(-73.65, 153.51) * mm});
            skArc(sketch, "E691", {"start": v(-73.65, 153.51) * mm, "mid": v(-73.82, 153.65) * mm, "end": v(-74, 153.75) * mm});
            skArc(sketch, "E692", {"start": v(-74, 153.75) * mm, "mid": v(-74.24, 153.85) * mm, "end": v(-74.48, 153.91) * mm});
            skArc(sketch, "E693", {"start": v(-74.48, 153.91) * mm, "mid": v(-74.66, 153.94) * mm, "end": v(-74.85, 153.95) * mm});
            skLineSegment(sketch, "E694", {"start": v(-74.85, 153.95) * mm, "end": v(-81.86, 153.95) * mm});
            skArc(sketch, "E695", {"start": v(-81.86, 153.95) * mm, "mid": v(-82.13, 153.93) * mm, "end": v(-82.4, 153.88) * mm});
            skArc(sketch, "E696", {"start": v(-82.4, 153.88) * mm, "mid": v(-82.62, 153.8) * mm, "end": v(-82.83, 153.69) * mm});
            skArc(sketch, "E697", {"start": v(-82.83, 153.69) * mm, "mid": v(-83, 153.57) * mm, "end": v(-83.14, 153.44) * mm});
            skArc(sketch, "E698", {"start": v(-83.14, 153.44) * mm, "mid": v(-83.25, 153.3) * mm, "end": v(-83.33, 153.17) * mm});
            skArc(sketch, "E699", {"start": v(-83.33, 153.17) * mm, "mid": v(-83.38, 153.04) * mm, "end": v(-83.42, 152.91) * mm});
            skArc(sketch, "E700", {"start": v(-83.42, 152.91) * mm, "mid": v(-83.43, 152.82) * mm, "end": v(-83.44, 152.73) * mm});
            skLineSegment(sketch, "E701", {"start": v(-83.44, 159.02) * mm, "end": v(-83.44, 158.04) * mm});
            skArc(sketch, "E702", {"start": v(-83.44, 158.04) * mm, "mid": v(-83.43, 157.9) * mm, "end": v(-83.4, 157.78) * mm});
            skArc(sketch, "E703", {"start": v(-83.4, 157.78) * mm, "mid": v(-83.35, 157.64) * mm, "end": v(-83.28, 157.51) * mm});
            skArc(sketch, "E704", {"start": v(-83.28, 157.51) * mm, "mid": v(-83.18, 157.37) * mm, "end": v(-83.06, 157.25) * mm});
            skArc(sketch, "E705", {"start": v(-83.06, 157.25) * mm, "mid": v(-82.9, 157.12) * mm, "end": v(-82.71, 157.01) * mm});
            skArc(sketch, "E706", {"start": v(-82.71, 157.01) * mm, "mid": v(-82.48, 156.91) * mm, "end": v(-82.23, 156.85) * mm});
            skArc(sketch, "E707", {"start": v(-82.23, 156.85) * mm, "mid": v(-82.05, 156.83) * mm, "end": v(-81.86, 156.82) * mm});
            skLineSegment(sketch, "E708", {"start": v(-81.86, 156.82) * mm, "end": v(-74.85, 156.82) * mm});
            skArc(sketch, "E709", {"start": v(-74.85, 156.82) * mm, "mid": v(-74.58, 156.84) * mm, "end": v(-74.32, 156.89) * mm});
            skArc(sketch, "E710", {"start": v(-74.32, 156.89) * mm, "mid": v(-74.1, 156.97) * mm, "end": v(-73.88, 157.08) * mm});
            skArc(sketch, "E711", {"start": v(-73.88, 157.08) * mm, "mid": v(-73.72, 157.2) * mm, "end": v(-73.57, 157.33) * mm});
            skArc(sketch, "E712", {"start": v(-73.57, 157.33) * mm, "mid": v(-73.47, 157.45) * mm, "end": v(-73.38, 157.6) * mm});
            skArc(sketch, "E713", {"start": v(-73.38, 157.6) * mm, "mid": v(-73.33, 157.72) * mm, "end": v(-73.3, 157.85) * mm});
            skArc(sketch, "E714", {"start": v(-73.3, 157.85) * mm, "mid": v(-73.28, 157.95) * mm, "end": v(-73.28, 158.04) * mm});
            skLineSegment(sketch, "E715", {"start": v(-73.28, 158.04) * mm, "end": v(-73.28, 159.02) * mm});
            skArc(sketch, "E716", {"start": v(-73.28, 159.02) * mm, "mid": v(-73.29, 159.15) * mm, "end": v(-73.31, 159.28) * mm});
            skArc(sketch, "E717", {"start": v(-73.31, 159.28) * mm, "mid": v(-73.36, 159.41) * mm, "end": v(-73.43, 159.54) * mm});
            skArc(sketch, "E718", {"start": v(-73.43, 159.54) * mm, "mid": v(-73.53, 159.68) * mm, "end": v(-73.65, 159.8) * mm});
            skArc(sketch, "E719", {"start": v(-73.65, 159.8) * mm, "mid": v(-73.82, 159.94) * mm, "end": v(-74, 160.04) * mm});
            skArc(sketch, "E720", {"start": v(-74, 160.04) * mm, "mid": v(-74.24, 160.14) * mm, "end": v(-74.48, 160.2) * mm});
            skArc(sketch, "E721", {"start": v(-74.48, 160.2) * mm, "mid": v(-74.66, 160.23) * mm, "end": v(-74.85, 160.24) * mm});
            skLineSegment(sketch, "E722", {"start": v(-74.85, 160.24) * mm, "end": v(-81.86, 160.24) * mm});
            skArc(sketch, "E723", {"start": v(-81.86, 160.24) * mm, "mid": v(-82.13, 160.22) * mm, "end": v(-82.4, 160.17) * mm});
            skArc(sketch, "E724", {"start": v(-82.4, 160.17) * mm, "mid": v(-82.62, 160.09) * mm, "end": v(-82.83, 159.98) * mm});
            skArc(sketch, "E725", {"start": v(-82.83, 159.98) * mm, "mid": v(-83, 159.86) * mm, "end": v(-83.14, 159.73) * mm});
            skArc(sketch, "E726", {"start": v(-83.14, 159.73) * mm, "mid": v(-83.25, 159.6) * mm, "end": v(-83.33, 159.46) * mm});
            skArc(sketch, "E727", {"start": v(-83.33, 159.46) * mm, "mid": v(-83.38, 159.33) * mm, "end": v(-83.42, 159.2) * mm});
            skArc(sketch, "E728", {"start": v(-83.42, 159.2) * mm, "mid": v(-83.43, 159.1) * mm, "end": v(-83.44, 159.02) * mm});
            skLineSegment(sketch, "E729", {"start": v(-91.8, 26.97) * mm, "end": v(-91.8, 31.52) * mm});
            skArc(sketch, "E730", {"start": v(-89.9, 33.41) * mm, "mid": v(-91.24, 32.86) * mm, "end": v(-91.8, 31.52) * mm});
            skLineSegment(sketch, "E731", {"start": v(-89.9, 33.41) * mm, "end": v(-55.77, 33.41) * mm});
            skLineSegment(sketch, "E732", {"start": v(-55.77, 33.41) * mm, "end": v(-55.77, 220.9) * mm});
            skLineSegment(sketch, "E733", {"start": v(-55.77, 220.9) * mm, "end": v(-89.9, 220.9) * mm});
            skArc(sketch, "E734", {"start": v(-91.8, 222.78) * mm, "mid": v(-91.24, 221.45) * mm, "end": v(-89.9, 220.9) * mm});
            skLineSegment(sketch, "E735", {"start": v(-91.8, 222.78) * mm, "end": v(-91.8, 228.38) * mm});
            skArc(sketch, "E736", {"start": v(-91.8, 228.38) * mm, "mid": v(-91.8, 228.53) * mm, "end": v(-91.84, 228.68) * mm});
            skArc(sketch, "E737", {"start": v(-91.84, 228.68) * mm, "mid": v(-91.9, 228.84) * mm, "end": v(-91.98, 228.99) * mm});
            skArc(sketch, "E738", {"start": v(-91.98, 228.99) * mm, "mid": v(-92.1, 229.15) * mm, "end": v(-92.25, 229.29) * mm});
            skArc(sketch, "E739", {"start": v(-92.25, 229.29) * mm, "mid": v(-92.45, 229.44) * mm, "end": v(-92.67, 229.56) * mm});
            skArc(sketch, "E740", {"start": v(-92.67, 229.56) * mm, "mid": v(-92.96, 229.68) * mm, "end": v(-93.26, 229.75) * mm});
            skArc(sketch, "E741", {"start": v(-93.26, 229.75) * mm, "mid": v(-93.47, 229.78) * mm, "end": v(-93.69, 229.79) * mm});
            skLineSegment(sketch, "E742", {"start": v(-93.69, 229.79) * mm, "end": v(-99.86, 229.79) * mm});
            skArc(sketch, "E743", {"start": v(-99.86, 229.79) * mm, "mid": v(-100.2, 229.76) * mm, "end": v(-100.53, 229.7) * mm});
            skArc(sketch, "E744", {"start": v(-100.53, 229.7) * mm, "mid": v(-100.8, 229.6) * mm, "end": v(-101.06, 229.46) * mm});
            skArc(sketch, "E745", {"start": v(-101.06, 229.46) * mm, "mid": v(-101.25, 229.32) * mm, "end": v(-101.42, 229.16) * mm});
            skArc(sketch, "E746", {"start": v(-101.42, 229.16) * mm, "mid": v(-101.54, 229.02) * mm, "end": v(-101.63, 228.86) * mm});
            skArc(sketch, "E747", {"start": v(-101.63, 228.86) * mm, "mid": v(-101.69, 228.72) * mm, "end": v(-101.73, 228.56) * mm});
            skArc(sketch, "E748", {"start": v(-101.73, 228.56) * mm, "mid": v(-101.74, 228.47) * mm, "end": v(-101.74, 228.38) * mm});
            skLineSegment(sketch, "E749", {"start": v(-101.74, 228.38) * mm, "end": v(-101.74, 222.78) * mm});
            skArc(sketch, "E750", {"start": v(-103.63, 220.9) * mm, "mid": v(-102.3, 221.45) * mm, "end": v(-101.74, 222.78) * mm});
            skLineSegment(sketch, "E751", {"start": v(-103.63, 220.9) * mm, "end": v(-137.78, 220.9) * mm});
            skLineSegment(sketch, "E752", {"start": v(-137.78, 220.9) * mm, "end": v(-137.78, 33.41) * mm});
            skLineSegment(sketch, "E753", {"start": v(-137.78, 33.41) * mm, "end": v(-103.63, 33.41) * mm});
            skArc(sketch, "E754", {"start": v(-101.74, 31.52) * mm, "mid": v(-102.3, 32.86) * mm, "end": v(-103.63, 33.41) * mm});
            skLineSegment(sketch, "E755", {"start": v(-101.74, 31.52) * mm, "end": v(-101.74, 26.97) * mm});
            skArc(sketch, "E756", {"start": v(-73.75, 75.17) * mm, "mid": v(-73.07, 76.5) * mm, "end": v(-72.59, 77.9) * mm});
            skLineSegment(sketch, "E757", {"start": v(-72.59, 77.9) * mm, "end": v(-72.59, 83.06) * mm});
            skArc(sketch, "E758", {"start": v(-72.59, 83.06) * mm, "mid": v(-73.07, 84.46) * mm, "end": v(-73.75, 85.78) * mm});
            skLineSegment(sketch, "E759", {"start": v(-73.75, 85.78) * mm, "end": v(-73.75, 75.17) * mm});
            skArc(sketch, "E760", {"start": v(-76.04, 72.56) * mm, "mid": v(-75.44, 73.09) * mm, "end": v(-74.88, 73.66) * mm});
            skLineSegment(sketch, "E761", {"start": v(-74.88, 73.66) * mm, "end": v(-74.88, 87.3) * mm});
            skArc(sketch, "E762", {"start": v(-74.88, 87.3) * mm, "mid": v(-75.44, 87.86) * mm, "end": v(-76.04, 88.39) * mm});
            skLineSegment(sketch, "E763", {"start": v(-76.04, 88.39) * mm, "end": v(-76.04, 72.56) * mm});
            skArc(sketch, "E764", {"start": v(-78.34, 71.17) * mm, "mid": v(-77.75, 71.45) * mm, "end": v(-77.18, 71.77) * mm});
            skLineSegment(sketch, "E765", {"start": v(-77.18, 71.77) * mm, "end": v(-77.18, 89.18) * mm});
            skArc(sketch, "E766", {"start": v(-77.18, 89.18) * mm, "mid": v(-77.75, 89.5) * mm, "end": v(-78.34, 89.78) * mm});
            skLineSegment(sketch, "E767", {"start": v(-78.34, 89.78) * mm, "end": v(-78.34, 71.17) * mm});
            skArc(sketch, "E768", {"start": v(-80.63, 70.48) * mm, "mid": v(-80.05, 70.6) * mm, "end": v(-79.47, 70.75) * mm});
            skLineSegment(sketch, "E769", {"start": v(-79.47, 70.75) * mm, "end": v(-79.47, 90.2) * mm});
            skArc(sketch, "E770", {"start": v(-79.47, 90.2) * mm, "mid": v(-80.05, 90.35) * mm, "end": v(-80.63, 90.48) * mm});
            skLineSegment(sketch, "E771", {"start": v(-80.63, 90.48) * mm, "end": v(-80.63, 70.48) * mm});
            skArc(sketch, "E772", {"start": v(-82.93, 70.33) * mm, "mid": v(-82.35, 70.32) * mm, "end": v(-81.77, 70.34) * mm});
            skLineSegment(sketch, "E773", {"start": v(-81.77, 70.34) * mm, "end": v(-81.77, 90.61) * mm});
            skArc(sketch, "E774", {"start": v(-81.77, 90.61) * mm, "mid": v(-82.35, 90.63) * mm, "end": v(-82.93, 90.62) * mm});
            skLineSegment(sketch, "E775", {"start": v(-82.93, 90.62) * mm, "end": v(-82.93, 70.33) * mm});
            skLineSegment(sketch, "E776", {"start": v(-84.06, 70.46) * mm, "end": v(-84.06, 90.5) * mm});
            skArc(sketch, "E777", {"start": v(-84.06, 90.5) * mm, "mid": v(-84.65, 90.38) * mm, "end": v(-85.22, 90.23) * mm});
            skLineSegment(sketch, "E778", {"start": v(-85.22, 90.23) * mm, "end": v(-85.22, 70.72) * mm});
            skArc(sketch, "E779", {"start": v(-85.22, 70.72) * mm, "mid": v(-84.65, 70.57) * mm, "end": v(-84.06, 70.46) * mm});
            skLineSegment(sketch, "E780", {"start": v(-86.36, 71.12) * mm, "end": v(-86.36, 89.83) * mm});
            skArc(sketch, "E781", {"start": v(-86.36, 89.83) * mm, "mid": v(-86.95, 89.56) * mm, "end": v(-87.52, 89.25) * mm});
            skLineSegment(sketch, "E782", {"start": v(-87.52, 89.25) * mm, "end": v(-87.52, 71.7) * mm});
            skArc(sketch, "E783", {"start": v(-87.52, 71.7) * mm, "mid": v(-86.95, 71.39) * mm, "end": v(-86.36, 71.12) * mm});
            skLineSegment(sketch, "E784", {"start": v(-88.65, 72.46) * mm, "end": v(-88.65, 88.49) * mm});
            skArc(sketch, "E785", {"start": v(-88.65, 88.49) * mm, "mid": v(-89.25, 87.98) * mm, "end": v(-89.81, 87.43) * mm});
            skLineSegment(sketch, "E786", {"start": v(-89.81, 87.43) * mm, "end": v(-89.81, 73.52) * mm});
            skArc(sketch, "E787", {"start": v(-89.81, 73.52) * mm, "mid": v(-89.25, 72.97) * mm, "end": v(-88.65, 72.46) * mm});
            skLineSegment(sketch, "E788", {"start": v(-90.94, 74.97) * mm, "end": v(-90.94, 85.98) * mm});
            skArc(sketch, "E789", {"start": v(-90.94, 85.98) * mm, "mid": v(-91.6, 84.78) * mm, "end": v(-92.1, 83.5) * mm});
            skLineSegment(sketch, "E790", {"start": v(-92.1, 83.5) * mm, "end": v(-92.1, 77.46) * mm});
            skArc(sketch, "E791", {"start": v(-92.1, 77.46) * mm, "mid": v(-91.6, 76.17) * mm, "end": v(-90.94, 74.97) * mm});
            skLineSegment(sketch, "E792", {"start": v(-44.04, 206.79) * mm, "end": v(-44.04, 33.72) * mm});
            skArc(sketch, "E793", {"start": v(-44.04, 33.72) * mm, "mid": v(-43.46, 32.31) * mm, "end": v(-42.04, 31.72) * mm});
            skLineSegment(sketch, "E794", {"start": v(-42.04, 31.72) * mm, "end": v(-41.1, 31.72) * mm});
            skArc(sketch, "E795", {"start": v(-41.1, 31.72) * mm, "mid": v(-39.7, 32.31) * mm, "end": v(-39.1, 33.72) * mm});
            skLineSegment(sketch, "E796", {"start": v(-39.1, 33.72) * mm, "end": v(-39.1, 206.79) * mm});
            skArc(sketch, "E797", {"start": v(-39.1, 206.79) * mm, "mid": v(-39.7, 208.2) * mm, "end": v(-41.1, 208.79) * mm});
            skLineSegment(sketch, "E798", {"start": v(-41.1, 208.79) * mm, "end": v(-42.04, 208.79) * mm});
            skArc(sketch, "E799", {"start": v(-42.04, 208.79) * mm, "mid": v(-43.46, 208.2) * mm, "end": v(-44.04, 206.79) * mm});
            skLineSegment(sketch, "E800", {"start": v(113.96, 197.18) * mm, "end": v(113.03, 197.18) * mm});
            skArc(sketch, "E801", {"start": v(113.03, 197.18) * mm, "mid": v(112.72, 197.16) * mm, "end": v(112.42, 197.1) * mm});
            skArc(sketch, "E802", {"start": v(112.42, 197.1) * mm, "mid": v(112.14, 197) * mm, "end": v(111.88, 196.86) * mm});
            skArc(sketch, "E803", {"start": v(111.88, 196.86) * mm, "mid": v(111.66, 196.7) * mm, "end": v(111.46, 196.52) * mm});
            skArc(sketch, "E804", {"start": v(111.46, 196.52) * mm, "mid": v(111.31, 196.33) * mm, "end": v(111.19, 196.12) * mm});
            skArc(sketch, "E805", {"start": v(111.19, 196.12) * mm, "mid": v(111.1, 195.92) * mm, "end": v(111.05, 195.7) * mm});
            skArc(sketch, "E806", {"start": v(111.05, 195.7) * mm, "mid": v(111.03, 195.57) * mm, "end": v(111.03, 195.44) * mm});
            skLineSegment(sketch, "E807", {"start": v(111.03, 195.44) * mm, "end": v(111.03, 44.88) * mm});
            skArc(sketch, "E808", {"start": v(111.03, 44.88) * mm, "mid": v(111.04, 44.66) * mm, "end": v(111.09, 44.45) * mm});
            skArc(sketch, "E809", {"start": v(111.09, 44.45) * mm, "mid": v(111.17, 44.24) * mm, "end": v(111.27, 44.05) * mm});
            skArc(sketch, "E810", {"start": v(111.27, 44.05) * mm, "mid": v(111.42, 43.85) * mm, "end": v(111.59, 43.67) * mm});
            skArc(sketch, "E811", {"start": v(111.59, 43.67) * mm, "mid": v(111.8, 43.5) * mm, "end": v(112.04, 43.36) * mm});
            skArc(sketch, "E812", {"start": v(112.04, 43.36) * mm, "mid": v(112.31, 43.25) * mm, "end": v(112.6, 43.18) * mm});
            skArc(sketch, "E813", {"start": v(112.6, 43.18) * mm, "mid": v(112.81, 43.15) * mm, "end": v(113.03, 43.14) * mm});
            skLineSegment(sketch, "E814", {"start": v(113.03, 43.14) * mm, "end": v(113.96, 43.14) * mm});
            skArc(sketch, "E815", {"start": v(113.96, 43.14) * mm, "mid": v(114.27, 43.16) * mm, "end": v(114.58, 43.22) * mm});
            skArc(sketch, "E816", {"start": v(114.58, 43.22) * mm, "mid": v(114.85, 43.32) * mm, "end": v(115.11, 43.45) * mm});
            skArc(sketch, "E817", {"start": v(115.11, 43.45) * mm, "mid": v(115.33, 43.6) * mm, "end": v(115.53, 43.8) * mm});
            skArc(sketch, "E818", {"start": v(115.53, 43.8) * mm, "mid": v(115.68, 43.98) * mm, "end": v(115.8, 44.2) * mm});
            skArc(sketch, "E819", {"start": v(115.8, 44.2) * mm, "mid": v(115.89, 44.4) * mm, "end": v(115.94, 44.61) * mm});
            skArc(sketch, "E820", {"start": v(115.94, 44.61) * mm, "mid": v(115.96, 44.74) * mm, "end": v(115.96, 44.88) * mm});
            skLineSegment(sketch, "E821", {"start": v(115.96, 44.88) * mm, "end": v(115.96, 195.44) * mm});
            skArc(sketch, "E822", {"start": v(115.96, 195.44) * mm, "mid": v(115.95, 195.65) * mm, "end": v(115.9, 195.86) * mm});
            skArc(sketch, "E823", {"start": v(115.9, 195.86) * mm, "mid": v(115.83, 196.07) * mm, "end": v(115.72, 196.27) * mm});
            skArc(sketch, "E824", {"start": v(115.72, 196.27) * mm, "mid": v(115.58, 196.46) * mm, "end": v(115.4, 196.64) * mm});
            skArc(sketch, "E825", {"start": v(115.4, 196.64) * mm, "mid": v(115.2, 196.8) * mm, "end": v(114.95, 196.95) * mm});
            skArc(sketch, "E826", {"start": v(114.95, 196.95) * mm, "mid": v(114.68, 197.06) * mm, "end": v(114.4, 197.14) * mm});
            skArc(sketch, "E827", {"start": v(114.4, 197.14) * mm, "mid": v(114.18, 197.17) * mm, "end": v(113.96, 197.18) * mm});
            skLineSegment(sketch, "E828", {"start": v(-33.54, 206.79) * mm, "end": v(-33.54, 33.72) * mm});
            skArc(sketch, "E829", {"start": v(-33.54, 33.72) * mm, "mid": v(-32.96, 32.31) * mm, "end": v(-31.54, 31.72) * mm});
            skLineSegment(sketch, "E830", {"start": v(-31.54, 31.72) * mm, "end": v(-30.6, 31.72) * mm});
            skArc(sketch, "E831", {"start": v(-30.6, 31.72) * mm, "mid": v(-29.2, 32.31) * mm, "end": v(-28.6, 33.72) * mm});
            skLineSegment(sketch, "E832", {"start": v(-28.6, 33.72) * mm, "end": v(-28.6, 206.79) * mm});
            skArc(sketch, "E833", {"start": v(-28.6, 206.79) * mm, "mid": v(-29.2, 208.2) * mm, "end": v(-30.6, 208.79) * mm});
            skLineSegment(sketch, "E834", {"start": v(-30.6, 208.79) * mm, "end": v(-31.54, 208.79) * mm});
            skArc(sketch, "E835", {"start": v(-31.54, 208.79) * mm, "mid": v(-32.96, 208.2) * mm, "end": v(-33.54, 206.79) * mm});
            skLineSegment(sketch, "E836", {"start": v(103.46, 197.18) * mm, "end": v(102.53, 197.18) * mm});
            skArc(sketch, "E837", {"start": v(102.53, 197.18) * mm, "mid": v(102.22, 197.16) * mm, "end": v(101.92, 197.1) * mm});
            skArc(sketch, "E838", {"start": v(101.92, 197.1) * mm, "mid": v(101.64, 197) * mm, "end": v(101.38, 196.86) * mm});
            skArc(sketch, "E839", {"start": v(101.38, 196.86) * mm, "mid": v(101.16, 196.7) * mm, "end": v(100.96, 196.52) * mm});
            skArc(sketch, "E840", {"start": v(100.96, 196.52) * mm, "mid": v(100.81, 196.33) * mm, "end": v(100.69, 196.12) * mm});
            skArc(sketch, "E841", {"start": v(100.69, 196.12) * mm, "mid": v(100.6, 195.92) * mm, "end": v(100.55, 195.7) * mm});
            skArc(sketch, "E842", {"start": v(100.55, 195.7) * mm, "mid": v(100.53, 195.57) * mm, "end": v(100.53, 195.44) * mm});
            skLineSegment(sketch, "E843", {"start": v(100.53, 195.44) * mm, "end": v(100.53, 44.88) * mm});
            skArc(sketch, "E844", {"start": v(100.53, 44.88) * mm, "mid": v(100.54, 44.66) * mm, "end": v(100.59, 44.45) * mm});
            skArc(sketch, "E845", {"start": v(100.59, 44.45) * mm, "mid": v(100.67, 44.24) * mm, "end": v(100.77, 44.05) * mm});
            skArc(sketch, "E846", {"start": v(100.77, 44.05) * mm, "mid": v(100.92, 43.85) * mm, "end": v(101.09, 43.67) * mm});
            skArc(sketch, "E847", {"start": v(101.09, 43.67) * mm, "mid": v(101.3, 43.5) * mm, "end": v(101.54, 43.36) * mm});
            skArc(sketch, "E848", {"start": v(101.54, 43.36) * mm, "mid": v(101.81, 43.25) * mm, "end": v(102.1, 43.18) * mm});
            skArc(sketch, "E849", {"start": v(102.1, 43.18) * mm, "mid": v(102.31, 43.15) * mm, "end": v(102.53, 43.14) * mm});
            skLineSegment(sketch, "E850", {"start": v(102.53, 43.14) * mm, "end": v(103.46, 43.14) * mm});
            skArc(sketch, "E851", {"start": v(103.46, 43.14) * mm, "mid": v(103.77, 43.16) * mm, "end": v(104.08, 43.22) * mm});
            skArc(sketch, "E852", {"start": v(104.08, 43.22) * mm, "mid": v(104.35, 43.32) * mm, "end": v(104.61, 43.45) * mm});
            skArc(sketch, "E853", {"start": v(104.61, 43.45) * mm, "mid": v(104.83, 43.6) * mm, "end": v(105.03, 43.8) * mm});
            skArc(sketch, "E854", {"start": v(105.03, 43.8) * mm, "mid": v(105.18, 43.98) * mm, "end": v(105.3, 44.2) * mm});
            skArc(sketch, "E855", {"start": v(105.3, 44.2) * mm, "mid": v(105.39, 44.4) * mm, "end": v(105.44, 44.61) * mm});
            skArc(sketch, "E856", {"start": v(105.44, 44.61) * mm, "mid": v(105.46, 44.74) * mm, "end": v(105.46, 44.88) * mm});
            skLineSegment(sketch, "E857", {"start": v(105.46, 44.88) * mm, "end": v(105.46, 195.44) * mm});
            skArc(sketch, "E858", {"start": v(105.46, 195.44) * mm, "mid": v(105.45, 195.65) * mm, "end": v(105.4, 195.86) * mm});
            skArc(sketch, "E859", {"start": v(105.4, 195.86) * mm, "mid": v(105.33, 196.07) * mm, "end": v(105.22, 196.27) * mm});
            skArc(sketch, "E860", {"start": v(105.22, 196.27) * mm, "mid": v(105.08, 196.46) * mm, "end": v(104.9, 196.64) * mm});
            skArc(sketch, "E861", {"start": v(104.9, 196.64) * mm, "mid": v(104.7, 196.8) * mm, "end": v(104.45, 196.95) * mm});
            skArc(sketch, "E862", {"start": v(104.45, 196.95) * mm, "mid": v(104.18, 197.06) * mm, "end": v(103.9, 197.14) * mm});
            skArc(sketch, "E863", {"start": v(103.9, 197.14) * mm, "mid": v(103.68, 197.17) * mm, "end": v(103.46, 197.18) * mm});
            skLineSegment(sketch, "E864", {"start": v(120.67, 16.34) * mm, "end": v(120.67, 22.5) * mm});
            skLineSegment(sketch, "E865", {"start": v(120.67, 22.5) * mm, "end": v(117.24, 22.5) * mm});
            skLineSegment(sketch, "E866", {"start": v(117.24, 22.5) * mm, "end": v(117.24, 24.1) * mm});
            skLineSegment(sketch, "E867", {"start": v(117.24, 24.1) * mm, "end": v(120.67, 24.1) * mm});
            skLineSegment(sketch, "E868", {"start": v(120.67, 24.1) * mm, "end": v(120.68, 35.63) * mm});
            skLineSegment(sketch, "E869", {"start": v(120.68, 35.63) * mm, "end": v(105.32, 35.63) * mm});
            skArc(sketch, "E870", {"start": v(103.71, 35.73) * mm, "mid": v(104.52, 35.65) * mm, "end": v(105.32, 35.63) * mm});
            skArc(sketch, "E871", {"start": v(101.78, 36.2) * mm, "mid": v(102.73, 35.9) * mm, "end": v(103.71, 35.73) * mm});
            skArc(sketch, "E872", {"start": v(101.14, 36.55) * mm, "mid": v(101.45, 36.35) * mm, "end": v(101.78, 36.2) * mm});
            skArc(sketch, "E873", {"start": v(100.9, 36.8) * mm, "mid": v(101.01, 36.66) * mm, "end": v(101.14, 36.55) * mm});
            skArc(sketch, "E874", {"start": v(100.82, 36.97) * mm, "mid": v(100.86, 36.88) * mm, "end": v(100.9, 36.8) * mm});
            skArc(sketch, "E875", {"start": v(100.8, 37.13) * mm, "mid": v(100.8, 37.05) * mm, "end": v(100.82, 36.97) * mm});
            skLineSegment(sketch, "E876", {"start": v(100.8, 37.13) * mm, "end": v(100.8, 38.06) * mm});
            skArc(sketch, "E877", {"start": v(100.8, 38.13) * mm, "mid": v(100.8, 38.1) * mm, "end": v(100.8, 38.06) * mm});
            skArc(sketch, "E878", {"start": v(100.84, 38.29) * mm, "mid": v(100.81, 38.21) * mm, "end": v(100.8, 38.13) * mm});
            skArc(sketch, "E879", {"start": v(100.98, 38.5) * mm, "mid": v(100.9, 38.4) * mm, "end": v(100.84, 38.29) * mm});
            skArc(sketch, "E880", {"start": v(101.34, 38.78) * mm, "mid": v(101.15, 38.65) * mm, "end": v(100.98, 38.5) * mm});
            skArc(sketch, "E881", {"start": v(102.43, 39.22) * mm, "mid": v(101.87, 39.03) * mm, "end": v(101.34, 38.78) * mm});
            skArc(sketch, "E882", {"start": v(105.32, 39.56) * mm, "mid": v(103.86, 39.48) * mm, "end": v(102.43, 39.22) * mm});
            skLineSegment(sketch, "E883", {"start": v(105.32, 39.56) * mm, "end": v(120.68, 39.56) * mm});
            skLineSegment(sketch, "E884", {"start": v(120.68, 39.56) * mm, "end": v(120.7, 200.73) * mm});
            skLineSegment(sketch, "E885", {"start": v(120.7, 200.73) * mm, "end": v(105.61, 200.73) * mm});
            skArc(sketch, "E886", {"start": v(103.99, 200.83) * mm, "mid": v(104.8, 200.75) * mm, "end": v(105.61, 200.73) * mm});
            skArc(sketch, "E887", {"start": v(102.13, 201.3) * mm, "mid": v(103.04, 201) * mm, "end": v(103.99, 200.83) * mm});
            skArc(sketch, "E888", {"start": v(101.5, 201.65) * mm, "mid": v(101.8, 201.45) * mm, "end": v(102.13, 201.3) * mm});
            skArc(sketch, "E889", {"start": v(101.27, 201.9) * mm, "mid": v(101.38, 201.76) * mm, "end": v(101.5, 201.65) * mm});
            skArc(sketch, "E890", {"start": v(101.18, 202.07) * mm, "mid": v(101.22, 201.98) * mm, "end": v(101.27, 201.9) * mm});
            skArc(sketch, "E891", {"start": v(101.16, 202.23) * mm, "mid": v(101.17, 202.15) * mm, "end": v(101.18, 202.07) * mm});
            skLineSegment(sketch, "E892", {"start": v(101.16, 202.23) * mm, "end": v(101.16, 203.16) * mm});
            skArc(sketch, "E893", {"start": v(101.16, 203.24) * mm, "mid": v(101.16, 203.2) * mm, "end": v(101.16, 203.16) * mm});
            skArc(sketch, "E894", {"start": v(101.22, 203.4) * mm, "mid": v(101.18, 203.33) * mm, "end": v(101.16, 203.24) * mm});
            skArc(sketch, "E895", {"start": v(101.36, 203.6) * mm, "mid": v(101.28, 203.51) * mm, "end": v(101.22, 203.4) * mm});
            skArc(sketch, "E896", {"start": v(101.72, 203.9) * mm, "mid": v(101.53, 203.76) * mm, "end": v(101.36, 203.6) * mm});
            skArc(sketch, "E897", {"start": v(102.8, 204.33) * mm, "mid": v(102.25, 204.15) * mm, "end": v(101.72, 203.9) * mm});
            skArc(sketch, "E898", {"start": v(105.61, 204.66) * mm, "mid": v(104.2, 204.59) * mm, "end": v(102.8, 204.33) * mm});
            skLineSegment(sketch, "E899", {"start": v(105.61, 204.66) * mm, "end": v(120.7, 204.66) * mm});
            skLineSegment(sketch, "E900", {"start": v(120.7, 204.66) * mm, "end": v(120.7, 216.2) * mm});
            skLineSegment(sketch, "E901", {"start": v(120.7, 216.2) * mm, "end": v(117.26, 216.2) * mm});
            skLineSegment(sketch, "E902", {"start": v(117.26, 216.2) * mm, "end": v(117.26, 217.8) * mm});
            skLineSegment(sketch, "E903", {"start": v(117.26, 217.8) * mm, "end": v(120.7, 217.8) * mm});
            skLineSegment(sketch, "E904", {"start": v(120.7, 217.8) * mm, "end": v(120.7, 231.81) * mm});
            skLineSegment(sketch, "E905", {"start": v(120.7, 231.81) * mm, "end": v(89.79, 231.81) * mm});
            skLineSegment(sketch, "E906", {"start": v(89.79, 231.81) * mm, "end": v(89.79, 217.81) * mm});
            skLineSegment(sketch, "E907", {"start": v(89.79, 217.81) * mm, "end": v(93.22, 217.81) * mm});
            skLineSegment(sketch, "E908", {"start": v(93.22, 217.81) * mm, "end": v(93.22, 216.21) * mm});
            skLineSegment(sketch, "E909", {"start": v(93.22, 216.21) * mm, "end": v(89.79, 216.21) * mm});
            skLineSegment(sketch, "E910", {"start": v(89.79, 216.21) * mm, "end": v(89.78, 192.85) * mm});
            skLineSegment(sketch, "E911", {"start": v(89.78, 192.85) * mm, "end": v(88.19, 192.85) * mm});
            skLineSegment(sketch, "E912", {"start": v(88.19, 192.85) * mm, "end": v(88.18, 164.14) * mm});
            skLineSegment(sketch, "E913", {"start": v(88.18, 164.14) * mm, "end": v(89.78, 164.14) * mm});
            skLineSegment(sketch, "E914", {"start": v(89.78, 164.14) * mm, "end": v(89.78, 117.6) * mm});
            skLineSegment(sketch, "E915", {"start": v(89.78, 117.6) * mm, "end": v(88.18, 117.6) * mm});
            skLineSegment(sketch, "E916", {"start": v(88.18, 117.6) * mm, "end": v(88.17, 88.88) * mm});
            skLineSegment(sketch, "E917", {"start": v(88.17, 88.88) * mm, "end": v(89.77, 88.88) * mm});
            skLineSegment(sketch, "E918", {"start": v(89.77, 88.88) * mm, "end": v(89.77, 65.55) * mm});
            skLineSegment(sketch, "E919", {"start": v(89.77, 65.55) * mm, "end": v(88.17, 65.55) * mm});
            skLineSegment(sketch, "E920", {"start": v(88.17, 65.55) * mm, "end": v(88.17, 44.6) * mm});
            skLineSegment(sketch, "E921", {"start": v(88.17, 44.6) * mm, "end": v(89.77, 44.6) * mm});
            skLineSegment(sketch, "E922", {"start": v(89.77, 44.6) * mm, "end": v(89.77, 24.1) * mm});
            skLineSegment(sketch, "E923", {"start": v(89.77, 24.1) * mm, "end": v(93.2, 24.1) * mm});
            skLineSegment(sketch, "E924", {"start": v(93.2, 24.1) * mm, "end": v(93.2, 22.5) * mm});
            skLineSegment(sketch, "E925", {"start": v(93.2, 22.5) * mm, "end": v(89.77, 22.5) * mm});
            skLineSegment(sketch, "E926", {"start": v(89.77, 22.5) * mm, "end": v(89.77, 16.34) * mm});
            skLineSegment(sketch, "E927", {"start": v(89.77, 16.34) * mm, "end": v(120.67, 16.34) * mm});
            skLineSegment(sketch, "E928", {"start": v(82.53, 16.34) * mm, "end": v(82.53, 22.5) * mm});
            skLineSegment(sketch, "E929", {"start": v(82.53, 22.5) * mm, "end": v(78.33, 22.5) * mm});
            skLineSegment(sketch, "E930", {"start": v(78.33, 22.5) * mm, "end": v(78.33, 24.1) * mm});
            skLineSegment(sketch, "E931", {"start": v(78.33, 24.1) * mm, "end": v(82.53, 24.1) * mm});
            skLineSegment(sketch, "E932", {"start": v(82.53, 24.1) * mm, "end": v(82.53, 44.6) * mm});
            skLineSegment(sketch, "E933", {"start": v(82.53, 44.6) * mm, "end": v(80.94, 44.6) * mm});
            skLineSegment(sketch, "E934", {"start": v(80.94, 44.6) * mm, "end": v(80.94, 65.55) * mm});
            skLineSegment(sketch, "E935", {"start": v(80.94, 65.55) * mm, "end": v(82.54, 65.55) * mm});
            skLineSegment(sketch, "E936", {"start": v(82.54, 65.55) * mm, "end": v(82.54, 88.88) * mm});
            skLineSegment(sketch, "E937", {"start": v(82.54, 88.88) * mm, "end": v(80.94, 88.88) * mm});
            skLineSegment(sketch, "E938", {"start": v(80.94, 88.88) * mm, "end": v(80.94, 117.6) * mm});
            skLineSegment(sketch, "E939", {"start": v(80.94, 117.6) * mm, "end": v(82.54, 117.6) * mm});
            skLineSegment(sketch, "E940", {"start": v(82.54, 117.6) * mm, "end": v(82.55, 164.14) * mm});
            skLineSegment(sketch, "E941", {"start": v(82.55, 164.14) * mm, "end": v(80.95, 164.14) * mm});
            skLineSegment(sketch, "E942", {"start": v(80.95, 164.14) * mm, "end": v(80.95, 192.85) * mm});
            skLineSegment(sketch, "E943", {"start": v(80.95, 192.85) * mm, "end": v(82.55, 192.85) * mm});
            skLineSegment(sketch, "E944", {"start": v(82.55, 192.85) * mm, "end": v(82.55, 216.21) * mm});
            skLineSegment(sketch, "E945", {"start": v(82.55, 216.21) * mm, "end": v(78.35, 216.21) * mm});
            skLineSegment(sketch, "E946", {"start": v(78.35, 216.21) * mm, "end": v(78.35, 217.81) * mm});
            skLineSegment(sketch, "E947", {"start": v(78.35, 217.81) * mm, "end": v(82.55, 217.81) * mm});
            skLineSegment(sketch, "E948", {"start": v(82.55, 217.81) * mm, "end": v(82.55, 231.81) * mm});
            skLineSegment(sketch, "E949", {"start": v(82.55, 231.81) * mm, "end": v(-8.16, 231.82) * mm});
            skLineSegment(sketch, "E950", {"start": v(-8.16, 231.82) * mm, "end": v(-8.16, 217.82) * mm});
            skLineSegment(sketch, "E951", {"start": v(-8.16, 217.82) * mm, "end": v(-4.01, 217.82) * mm});
            skLineSegment(sketch, "E952", {"start": v(-4.01, 217.82) * mm, "end": v(-4.01, 216.22) * mm});
            skLineSegment(sketch, "E953", {"start": v(-4.01, 216.22) * mm, "end": v(-8.16, 216.22) * mm});
            skLineSegment(sketch, "E954", {"start": v(-8.16, 216.22) * mm, "end": v(-8.16, 192.86) * mm});
            skLineSegment(sketch, "E955", {"start": v(-8.16, 192.86) * mm, "end": v(-6.56, 192.86) * mm});
            skLineSegment(sketch, "E956", {"start": v(-6.56, 192.86) * mm, "end": v(-6.57, 164.14) * mm});
            skLineSegment(sketch, "E957", {"start": v(-6.57, 164.14) * mm, "end": v(-8.17, 164.14) * mm});
            skLineSegment(sketch, "E958", {"start": v(-8.17, 164.14) * mm, "end": v(-8.17, 117.6) * mm});
            skLineSegment(sketch, "E959", {"start": v(-8.17, 117.6) * mm, "end": v(-6.57, 117.6) * mm});
            skLineSegment(sketch, "E960", {"start": v(-6.57, 117.6) * mm, "end": v(-6.57, 88.89) * mm});
            skLineSegment(sketch, "E961", {"start": v(-6.57, 88.89) * mm, "end": v(-8.17, 88.89) * mm});
            skLineSegment(sketch, "E962", {"start": v(-8.17, 88.89) * mm, "end": v(-8.18, 65.56) * mm});
            skLineSegment(sketch, "E963", {"start": v(-8.18, 65.56) * mm, "end": v(-6.58, 65.56) * mm});
            skLineSegment(sketch, "E964", {"start": v(-6.58, 65.56) * mm, "end": v(-6.58, 36.84) * mm});
            skLineSegment(sketch, "E965", {"start": v(-6.58, 36.84) * mm, "end": v(-8.18, 36.84) * mm});
            skLineSegment(sketch, "E966", {"start": v(-8.18, 36.84) * mm, "end": v(-8.18, 24.1) * mm});
            skLineSegment(sketch, "E967", {"start": v(-8.18, 24.1) * mm, "end": v(-4.04, 24.1) * mm});
            skLineSegment(sketch, "E968", {"start": v(-4.04, 24.1) * mm, "end": v(-4.04, 22.5) * mm});
            skLineSegment(sketch, "E969", {"start": v(-4.04, 22.5) * mm, "end": v(-8.18, 22.5) * mm});
            skLineSegment(sketch, "E970", {"start": v(-8.18, 22.5) * mm, "end": v(-8.18, 16.35) * mm});
            skLineSegment(sketch, "E971", {"start": v(-8.18, 16.35) * mm, "end": v(82.53, 16.34) * mm});
            skLineSegment(sketch, "E972", {"start": v(-17.87, 16.46) * mm, "end": v(-17.87, 22.61) * mm});
            skLineSegment(sketch, "E973", {"start": v(-17.87, 22.61) * mm, "end": v(-21.3, 22.61) * mm});
            skLineSegment(sketch, "E974", {"start": v(-21.3, 22.61) * mm, "end": v(-21.3, 24.21) * mm});
            skLineSegment(sketch, "E975", {"start": v(-21.3, 24.21) * mm, "end": v(-17.87, 24.21) * mm});
            skLineSegment(sketch, "E976", {"start": v(-17.87, 24.21) * mm, "end": v(-17.86, 36.94) * mm});
            skLineSegment(sketch, "E977", {"start": v(-17.86, 36.94) * mm, "end": v(-16.27, 36.94) * mm});
            skLineSegment(sketch, "E978", {"start": v(-16.27, 36.94) * mm, "end": v(-16.26, 65.66) * mm});
            skLineSegment(sketch, "E979", {"start": v(-16.26, 65.66) * mm, "end": v(-17.86, 65.66) * mm});
            skLineSegment(sketch, "E980", {"start": v(-17.86, 65.66) * mm, "end": v(-17.86, 88.99) * mm});
            skLineSegment(sketch, "E981", {"start": v(-17.86, 88.99) * mm, "end": v(-16.26, 88.99) * mm});
            skLineSegment(sketch, "E982", {"start": v(-16.26, 88.99) * mm, "end": v(-16.26, 117.7) * mm});
            skLineSegment(sketch, "E983", {"start": v(-16.26, 117.7) * mm, "end": v(-17.86, 117.7) * mm});
            skLineSegment(sketch, "E984", {"start": v(-17.86, 117.7) * mm, "end": v(-17.85, 164.25) * mm});
            skLineSegment(sketch, "E985", {"start": v(-17.85, 164.25) * mm, "end": v(-16.25, 164.25) * mm});
            skLineSegment(sketch, "E986", {"start": v(-16.25, 164.25) * mm, "end": v(-16.25, 192.96) * mm});
            skLineSegment(sketch, "E987", {"start": v(-16.25, 192.96) * mm, "end": v(-17.85, 192.96) * mm});
            skLineSegment(sketch, "E988", {"start": v(-17.85, 192.96) * mm, "end": v(-17.85, 216.32) * mm});
            skLineSegment(sketch, "E989", {"start": v(-17.85, 216.32) * mm, "end": v(-21.28, 216.32) * mm});
            skLineSegment(sketch, "E990", {"start": v(-21.28, 216.32) * mm, "end": v(-21.28, 217.92) * mm});
            skLineSegment(sketch, "E991", {"start": v(-21.28, 217.92) * mm, "end": v(-17.84, 217.92) * mm});
            skLineSegment(sketch, "E992", {"start": v(-17.84, 217.92) * mm, "end": v(-17.84, 231.93) * mm});
            skLineSegment(sketch, "E993", {"start": v(-17.84, 231.93) * mm, "end": v(-48.75, 231.93) * mm});
            skLineSegment(sketch, "E994", {"start": v(-48.75, 231.93) * mm, "end": v(-48.75, 217.93) * mm});
            skLineSegment(sketch, "E995", {"start": v(-48.75, 217.93) * mm, "end": v(-45.38, 217.93) * mm});
            skLineSegment(sketch, "E996", {"start": v(-45.38, 217.93) * mm, "end": v(-45.38, 216.33) * mm});
            skLineSegment(sketch, "E997", {"start": v(-45.38, 216.33) * mm, "end": v(-48.75, 216.33) * mm});
            skLineSegment(sketch, "E998", {"start": v(-48.75, 216.33) * mm, "end": v(-48.77, 24.21) * mm});
            skLineSegment(sketch, "E999", {"start": v(-48.77, 24.21) * mm, "end": v(-45.4, 24.21) * mm});
            skLineSegment(sketch, "E1000", {"start": v(-45.4, 24.21) * mm, "end": v(-45.4, 22.61) * mm});
            skLineSegment(sketch, "E1001", {"start": v(-45.4, 22.61) * mm, "end": v(-48.77, 22.61) * mm});
            skLineSegment(sketch, "E1002", {"start": v(-48.77, 22.61) * mm, "end": v(-48.77, 16.46) * mm});
            skLineSegment(sketch, "E1003", {"start": v(-48.77, 16.46) * mm, "end": v(-17.87, 16.46) * mm});
            skCircle(sketch, "E1004", {"center": v(8.82, 227.54) * mm, "radius": 1.7 * mm});
            skCircle(sketch, "E1005", {"center": v(65.57, 227.53) * mm, "radius": 1.7 * mm});
            skCircle(sketch, "E1006", {"center": v(0.31, 19.34) * mm, "radius": 1.7 * mm});
            skCircle(sketch, "E1007", {"center": v(74.04, 19.34) * mm, "radius": 1.7 * mm});
            skLineSegment(sketch, "E1008", {"start": v(-101.74, 26.97) * mm, "end": v(-91.8, 26.97) * mm});
            skPoint(sketch, "E1009.endSnap0", {"position": v(-114.56, 186.03) * mm});
            skSolve(sketch);
        }
        {
            var Q0;
            Q0 = qSketchRegion(id + "F0", true);
            extrude(context, id + "F1", {"entities" : qUnion([Q0]), "depth" : 3 * mm});
        }
    });
